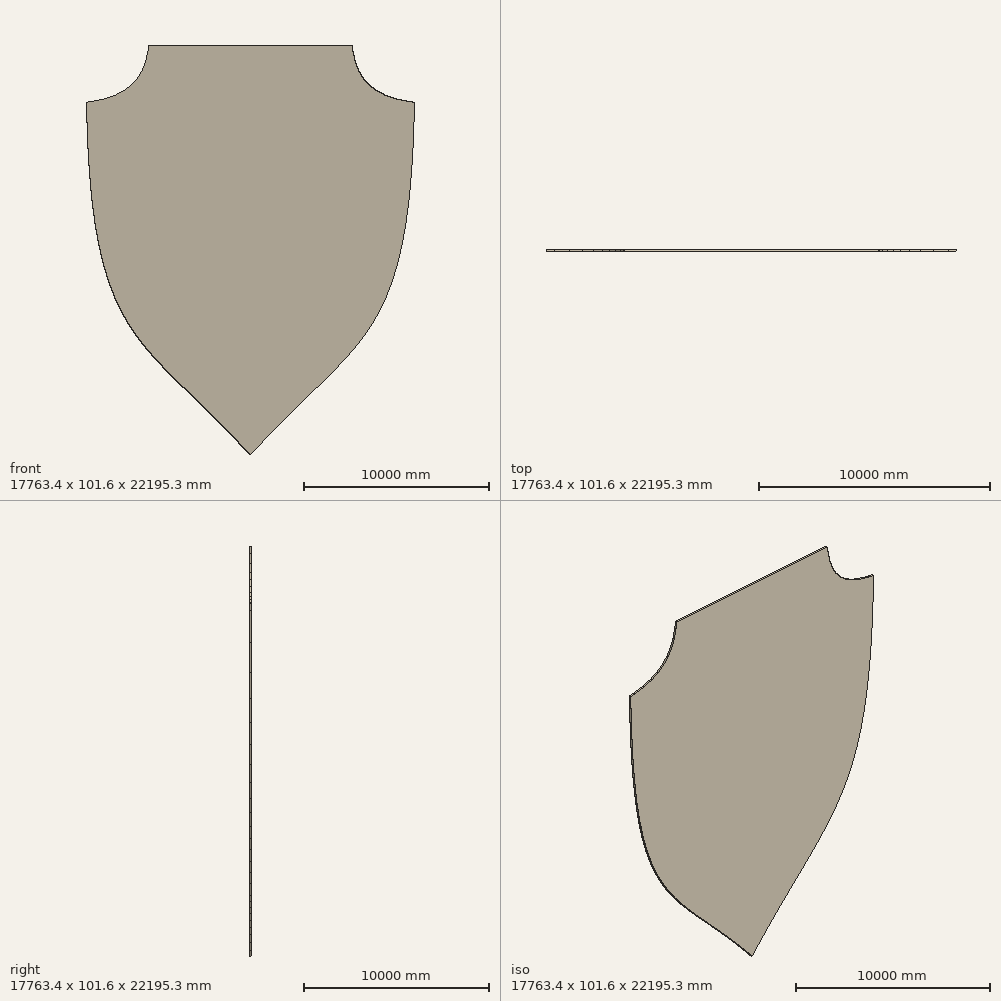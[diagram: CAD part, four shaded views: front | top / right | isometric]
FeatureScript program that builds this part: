
annotation { "Feature Type Name" : "Feature", "Feature Type Description" : "" }
export const myFeature = defineFeature(function(context is Context, id is Id, definition is map)
    precondition{}
    {
        {
            var Q0;
            Q0=qCreatedBy(makeId("Front.planeOp"),FACE);
            var sketch = newSketch(context, id + "F0", { "sketchPlane" : qUnion([Q0])});
            skLineSegment(sketch, "E0", {"start": v(3606.7, -2114.03) * mm, "end": v(3623.1, -2111.71) * mm});
            skLineSegment(sketch, "E1", {"start": v(3623.1, -2111.71) * mm, "end": v(3639.28, -2108.84) * mm});
            skLineSegment(sketch, "E2", {"start": v(3639.28, -2108.84) * mm, "end": v(3655.23, -2105.42) * mm});
            skLineSegment(sketch, "E3", {"start": v(3655.23, -2105.42) * mm, "end": v(3670.91, -2101.43) * mm});
            skLineSegment(sketch, "E4", {"start": v(3670.91, -2101.43) * mm, "end": v(3686.32, -2096.89) * mm});
            skLineSegment(sketch, "E5", {"start": v(3686.32, -2096.89) * mm, "end": v(3701.44, -2091.78) * mm});
            skLineSegment(sketch, "E6", {"start": v(3701.44, -2091.78) * mm, "end": v(3716.25, -2086.1) * mm});
            skLineSegment(sketch, "E7", {"start": v(3716.25, -2086.1) * mm, "end": v(3730.73, -2079.87) * mm});
            skLineSegment(sketch, "E8", {"start": v(3730.73, -2079.87) * mm, "end": v(3781.7, -2025.13) * mm});
            skLineSegment(sketch, "E9", {"start": v(3781.7, -2025.13) * mm, "end": v(3828.45, -1969.92) * mm});
            skLineSegment(sketch, "E10", {"start": v(3828.45, -1969.92) * mm, "end": v(3871.15, -1913.92) * mm});
            skLineSegment(sketch, "E11", {"start": v(3871.15, -1913.92) * mm, "end": v(3909.97, -1856.8) * mm});
            skLineSegment(sketch, "E12", {"start": v(3909.97, -1856.8) * mm, "end": v(3945.09, -1798.2) * mm});
            skLineSegment(sketch, "E13", {"start": v(3945.09, -1798.2) * mm, "end": v(3976.68, -1737.82) * mm});
            skLineSegment(sketch, "E14", {"start": v(3976.68, -1737.82) * mm, "end": v(4004.91, -1675.31) * mm});
            skLineSegment(sketch, "E15", {"start": v(4004.91, -1675.31) * mm, "end": v(4029.96, -1610.35) * mm});
            skLineSegment(sketch, "E16", {"start": v(4029.96, -1610.35) * mm, "end": v(4024.08, -1606.15) * mm});
            skLineSegment(sketch, "E17", {"start": v(4024.08, -1606.15) * mm, "end": v(4018.25, -1601.82) * mm});
            skLineSegment(sketch, "E18", {"start": v(4018.25, -1601.82) * mm, "end": v(4012.5, -1597.37) * mm});
            skLineSegment(sketch, "E19", {"start": v(4012.5, -1597.37) * mm, "end": v(4006.8, -1592.78) * mm});
            skLineSegment(sketch, "E20", {"start": v(4006.8, -1592.78) * mm, "end": v(4001.2, -1588.05) * mm});
            skLineSegment(sketch, "E21", {"start": v(4001.2, -1588.05) * mm, "end": v(3995.67, -1583.17) * mm});
            skLineSegment(sketch, "E22", {"start": v(3995.67, -1583.17) * mm, "end": v(3990.24, -1578.13) * mm});
            skLineSegment(sketch, "E23", {"start": v(3990.24, -1578.13) * mm, "end": v(3984.9, -1572.93) * mm});
            skLineSegment(sketch, "E24", {"start": v(3984.9, -1572.93) * mm, "end": v(3942.11, -1520.55) * mm});
            skLineSegment(sketch, "E25", {"start": v(3942.11, -1520.55) * mm, "end": v(3911.55, -1462.47) * mm});
            skLineSegment(sketch, "E26", {"start": v(3911.55, -1462.47) * mm, "end": v(3893.2, -1400.6) * mm});
            skLineSegment(sketch, "E27", {"start": v(3893.2, -1400.6) * mm, "end": v(3887.1, -1336.81) * mm});
            skLineSegment(sketch, "E28", {"start": v(3887.1, -1336.81) * mm, "end": v(3893.2, -1273.04) * mm});
            skLineSegment(sketch, "E29", {"start": v(3893.2, -1273.04) * mm, "end": v(3911.54, -1211.16) * mm});
            skLineSegment(sketch, "E30", {"start": v(3911.54, -1211.16) * mm, "end": v(3942.1, -1153.08) * mm});
            skLineSegment(sketch, "E31", {"start": v(3942.1, -1153.08) * mm, "end": v(3984.9, -1100.7) * mm});
            skLineSegment(sketch, "E32", {"start": v(3984.9, -1100.7) * mm, "end": v(4037.28, -1057.9) * mm});
            skLineSegment(sketch, "E33", {"start": v(4037.28, -1057.9) * mm, "end": v(4095.35, -1027.34) * mm});
            skLineSegment(sketch, "E34", {"start": v(4095.35, -1027.34) * mm, "end": v(4157.23, -1009) * mm});
            skLineSegment(sketch, "E35", {"start": v(4157.23, -1009) * mm, "end": v(4221, -1002.9) * mm});
            skLineSegment(sketch, "E36", {"start": v(4221, -1002.9) * mm, "end": v(4284.78, -1009) * mm});
            skLineSegment(sketch, "E37", {"start": v(4284.78, -1009) * mm, "end": v(4346.65, -1027.34) * mm});
            skLineSegment(sketch, "E38", {"start": v(4346.65, -1027.34) * mm, "end": v(4404.73, -1057.9) * mm});
            skLineSegment(sketch, "E39", {"start": v(4404.73, -1057.9) * mm, "end": v(4457.12, -1100.7) * mm});
            skLineSegment(sketch, "E40", {"start": v(4457.12, -1100.7) * mm, "end": v(4499.9, -1153.08) * mm});
            skLineSegment(sketch, "E41", {"start": v(4499.9, -1153.08) * mm, "end": v(4530.47, -1211.16) * mm});
            skLineSegment(sketch, "E42", {"start": v(4530.47, -1211.16) * mm, "end": v(4548.8, -1273.04) * mm});
            skLineSegment(sketch, "E43", {"start": v(4548.8, -1273.04) * mm, "end": v(4554.92, -1336.81) * mm});
            skLineSegment(sketch, "E44", {"start": v(4554.92, -1336.81) * mm, "end": v(4548.8, -1400.6) * mm});
            skLineSegment(sketch, "E45", {"start": v(4548.8, -1400.6) * mm, "end": v(4530.47, -1462.47) * mm});
            skLineSegment(sketch, "E46", {"start": v(4530.47, -1462.47) * mm, "end": v(4499.9, -1520.55) * mm});
            skLineSegment(sketch, "E47", {"start": v(4499.9, -1520.55) * mm, "end": v(4457.12, -1572.93) * mm});
            skLineSegment(sketch, "E48", {"start": v(4457.12, -1572.93) * mm, "end": v(4426.96, -1599.67) * mm});
            skLineSegment(sketch, "E49", {"start": v(4426.96, -1599.67) * mm, "end": v(4394.55, -1622.12) * mm});
            skLineSegment(sketch, "E50", {"start": v(4394.55, -1622.12) * mm, "end": v(4360.27, -1640.28) * mm});
            skLineSegment(sketch, "E51", {"start": v(4360.27, -1640.28) * mm, "end": v(4324.52, -1654.17) * mm});
            skLineSegment(sketch, "E52", {"start": v(4324.52, -1654.17) * mm, "end": v(4287.68, -1663.8) * mm});
            skLineSegment(sketch, "E53", {"start": v(4287.68, -1663.8) * mm, "end": v(4250.15, -1669.15) * mm});
            skLineSegment(sketch, "E54", {"start": v(4250.15, -1669.15) * mm, "end": v(4212.32, -1670.25) * mm});
            skLineSegment(sketch, "E55", {"start": v(4212.32, -1670.25) * mm, "end": v(4174.57, -1667.12) * mm});
            skLineSegment(sketch, "E56", {"start": v(4174.57, -1667.12) * mm, "end": v(4173.7, -1667.68) * mm});
            skLineSegment(sketch, "E57", {"start": v(4173.7, -1667.68) * mm, "end": v(4172.86, -1668.24) * mm});
            skLineSegment(sketch, "E58", {"start": v(4172.86, -1668.24) * mm, "end": v(4172.03, -1668.82) * mm});
            skLineSegment(sketch, "E59", {"start": v(4172.03, -1668.82) * mm, "end": v(4171.2, -1669.4) * mm});
            skLineSegment(sketch, "E60", {"start": v(4171.2, -1669.4) * mm, "end": v(4170.37, -1669.98) * mm});
            skLineSegment(sketch, "E61", {"start": v(4170.37, -1669.98) * mm, "end": v(4169.53, -1670.55) * mm});
            skLineSegment(sketch, "E62", {"start": v(4169.53, -1670.55) * mm, "end": v(4168.68, -1671.11) * mm});
            skLineSegment(sketch, "E63", {"start": v(4168.68, -1671.11) * mm, "end": v(4167.8, -1671.66) * mm});
            skLineSegment(sketch, "E64", {"start": v(4167.8, -1671.66) * mm, "end": v(4147.85, -1746.44) * mm});
            skLineSegment(sketch, "E65", {"start": v(4147.85, -1746.44) * mm, "end": v(4115.54, -1827.73) * mm});
            skLineSegment(sketch, "E66", {"start": v(4115.54, -1827.73) * mm, "end": v(4072.55, -1913.84) * mm});
            skLineSegment(sketch, "E67", {"start": v(4072.55, -1913.84) * mm, "end": v(4020.56, -2003.05) * mm});
            skLineSegment(sketch, "E68", {"start": v(4020.56, -2003.05) * mm, "end": v(3961.25, -2093.65) * mm});
            skLineSegment(sketch, "E69", {"start": v(3961.25, -2093.65) * mm, "end": v(3896.3, -2183.93) * mm});
            skLineSegment(sketch, "E70", {"start": v(3896.3, -2183.93) * mm, "end": v(3827.38, -2272.18) * mm});
            skLineSegment(sketch, "E71", {"start": v(3827.38, -2272.18) * mm, "end": v(3756.18, -2356.7) * mm});
            skLineSegment(sketch, "E72", {"start": v(3756.18, -2356.7) * mm, "end": v(4921.1, -3614.15) * mm});
            skLineSegment(sketch, "E73", {"start": v(4921.1, -3614.15) * mm, "end": v(4990.22, -3578.05) * mm});
            skLineSegment(sketch, "E74", {"start": v(4990.22, -3578.05) * mm, "end": v(5063.34, -3554.5) * mm});
            skLineSegment(sketch, "E75", {"start": v(5063.34, -3554.5) * mm, "end": v(5138.77, -3543.48) * mm});
            skLineSegment(sketch, "E76", {"start": v(5138.77, -3543.48) * mm, "end": v(5214.82, -3545.02) * mm});
            skLineSegment(sketch, "E77", {"start": v(5214.82, -3545.02) * mm, "end": v(5289.82, -3559.12) * mm});
            skLineSegment(sketch, "E78", {"start": v(5289.82, -3559.12) * mm, "end": v(5362.07, -3585.78) * mm});
            skLineSegment(sketch, "E79", {"start": v(5362.07, -3585.78) * mm, "end": v(5429.9, -3625.02) * mm});
            skLineSegment(sketch, "E80", {"start": v(5429.9, -3625.02) * mm, "end": v(5491.63, -3676.84) * mm});
            skLineSegment(sketch, "E81", {"start": v(5491.63, -3676.84) * mm, "end": v(5550.45, -3748.84) * mm});
            skLineSegment(sketch, "E82", {"start": v(5550.45, -3748.84) * mm, "end": v(5592.46, -3828.68) * mm});
            skLineSegment(sketch, "E83", {"start": v(5592.46, -3828.68) * mm, "end": v(5617.67, -3913.74) * mm});
            skLineSegment(sketch, "E84", {"start": v(5617.67, -3913.74) * mm, "end": v(5626.07, -4001.4) * mm});
            skLineSegment(sketch, "E85", {"start": v(5626.07, -4001.4) * mm, "end": v(5617.67, -4089.07) * mm});
            skLineSegment(sketch, "E86", {"start": v(5617.67, -4089.07) * mm, "end": v(5592.46, -4174.12) * mm});
            skLineSegment(sketch, "E87", {"start": v(5592.46, -4174.12) * mm, "end": v(5550.45, -4253.96) * mm});
            skLineSegment(sketch, "E88", {"start": v(5550.45, -4253.96) * mm, "end": v(5491.63, -4325.96) * mm});
            skLineSegment(sketch, "E89", {"start": v(5491.63, -4325.96) * mm, "end": v(5419.63, -4384.77) * mm});
            skLineSegment(sketch, "E90", {"start": v(5419.63, -4384.77) * mm, "end": v(5339.8, -4426.78) * mm});
            skLineSegment(sketch, "E91", {"start": v(5339.8, -4426.78) * mm, "end": v(5254.74, -4451.98) * mm});
            skLineSegment(sketch, "E92", {"start": v(5254.74, -4451.98) * mm, "end": v(5167.07, -4460.38) * mm});
            skLineSegment(sketch, "E93", {"start": v(5167.07, -4460.38) * mm, "end": v(5079.41, -4451.98) * mm});
            skLineSegment(sketch, "E94", {"start": v(5079.41, -4451.98) * mm, "end": v(4994.36, -4426.78) * mm});
            skLineSegment(sketch, "E95", {"start": v(4994.36, -4426.78) * mm, "end": v(4914.53, -4384.77) * mm});
            skLineSegment(sketch, "E96", {"start": v(4914.53, -4384.77) * mm, "end": v(4842.54, -4325.96) * mm});
            skLineSegment(sketch, "E97", {"start": v(4842.54, -4325.96) * mm, "end": v(4791.9, -4265.9) * mm});
            skLineSegment(sketch, "E98", {"start": v(4791.9, -4265.9) * mm, "end": v(4753.22, -4200.01) * mm});
            skLineSegment(sketch, "E99", {"start": v(4753.22, -4200.01) * mm, "end": v(4726.49, -4129.84) * mm});
            skLineSegment(sketch, "E100", {"start": v(4726.49, -4129.84) * mm, "end": v(4711.7, -4056.95) * mm});
            skLineSegment(sketch, "E101", {"start": v(4711.7, -4056.95) * mm, "end": v(4708.83, -3982.9) * mm});
            skLineSegment(sketch, "E102", {"start": v(4708.83, -3982.9) * mm, "end": v(4717.87, -3909.23) * mm});
            skLineSegment(sketch, "E103", {"start": v(4717.87, -3909.23) * mm, "end": v(4738.82, -3837.5) * mm});
            skLineSegment(sketch, "E104", {"start": v(4738.82, -3837.5) * mm, "end": v(4771.64, -3769.27) * mm});
            skLineSegment(sketch, "E105", {"start": v(4771.64, -3769.27) * mm, "end": v(3503.24, -2609.63) * mm});
            skLineSegment(sketch, "E106", {"start": v(3503.24, -2609.63) * mm, "end": v(3421.12, -2678.8) * mm});
            skLineSegment(sketch, "E107", {"start": v(3421.12, -2678.8) * mm, "end": v(3335.84, -2745.38) * mm});
            skLineSegment(sketch, "E108", {"start": v(3335.84, -2745.38) * mm, "end": v(3248.9, -2807.89) * mm});
            skLineSegment(sketch, "E109", {"start": v(3248.9, -2807.89) * mm, "end": v(3161.83, -2864.82) * mm});
            skLineSegment(sketch, "E110", {"start": v(3161.83, -2864.82) * mm, "end": v(3076.12, -2914.67) * mm});
            skLineSegment(sketch, "E111", {"start": v(3076.12, -2914.67) * mm, "end": v(2993.27, -2955.94) * mm});
            skLineSegment(sketch, "E112", {"start": v(2993.27, -2955.94) * mm, "end": v(2914.8, -2987.14) * mm});
            skLineSegment(sketch, "E113", {"start": v(2914.8, -2987.14) * mm, "end": v(2842.2, -3006.76) * mm});
            skLineSegment(sketch, "E114", {"start": v(2842.2, -3006.76) * mm, "end": v(2841.24, -3008.5) * mm});
            skLineSegment(sketch, "E115", {"start": v(2841.24, -3008.5) * mm, "end": v(2840.27, -3010.17) * mm});
            skLineSegment(sketch, "E116", {"start": v(2840.27, -3010.17) * mm, "end": v(2839.29, -3011.8) * mm});
            skLineSegment(sketch, "E117", {"start": v(2839.29, -3011.8) * mm, "end": v(2838.3, -3013.4) * mm});
            skLineSegment(sketch, "E118", {"start": v(2838.3, -3013.4) * mm, "end": v(2837.32, -3014.98) * mm});
            skLineSegment(sketch, "E119", {"start": v(2837.32, -3014.98) * mm, "end": v(2836.34, -3016.58) * mm});
            skLineSegment(sketch, "E120", {"start": v(2836.34, -3016.58) * mm, "end": v(2835.36, -3018.2) * mm});
            skLineSegment(sketch, "E121", {"start": v(2835.36, -3018.2) * mm, "end": v(2834.39, -3019.87) * mm});
            skLineSegment(sketch, "E122", {"start": v(2834.39, -3019.87) * mm, "end": v(2836.27, -3056.3) * mm});
            skLineSegment(sketch, "E123", {"start": v(2836.27, -3056.3) * mm, "end": v(2834.2, -3092.72) * mm});
            skLineSegment(sketch, "E124", {"start": v(2834.2, -3092.72) * mm, "end": v(2828.18, -3128.78) * mm});
            skLineSegment(sketch, "E125", {"start": v(2828.18, -3128.78) * mm, "end": v(2818.2, -3164.14) * mm});
            skLineSegment(sketch, "E126", {"start": v(2818.2, -3164.14) * mm, "end": v(2804.25, -3198.43) * mm});
            skLineSegment(sketch, "E127", {"start": v(2804.25, -3198.43) * mm, "end": v(2786.34, -3231.31) * mm});
            skLineSegment(sketch, "E128", {"start": v(2786.34, -3231.31) * mm, "end": v(2764.46, -3262.43) * mm});
            skLineSegment(sketch, "E129", {"start": v(2764.46, -3262.43) * mm, "end": v(2738.6, -3291.45) * mm});
            skLineSegment(sketch, "E130", {"start": v(2738.6, -3291.45) * mm, "end": v(2686.22, -3334.23) * mm});
            skLineSegment(sketch, "E131", {"start": v(2686.22, -3334.23) * mm, "end": v(2628.14, -3364.8) * mm});
            skLineSegment(sketch, "E132", {"start": v(2628.14, -3364.8) * mm, "end": v(2566.26, -3383.13) * mm});
            skLineSegment(sketch, "E133", {"start": v(2566.26, -3383.13) * mm, "end": v(2502.49, -3389.24) * mm});
            skLineSegment(sketch, "E134", {"start": v(2502.49, -3389.24) * mm, "end": v(2438.71, -3383.13) * mm});
            skLineSegment(sketch, "E135", {"start": v(2438.71, -3383.13) * mm, "end": v(2376.84, -3364.79) * mm});
            skLineSegment(sketch, "E136", {"start": v(2376.84, -3364.79) * mm, "end": v(2318.77, -3334.23) * mm});
            skLineSegment(sketch, "E137", {"start": v(2318.77, -3334.23) * mm, "end": v(2266.4, -3291.45) * mm});
            skLineSegment(sketch, "E138", {"start": v(2266.4, -3291.45) * mm, "end": v(2223.6, -3239.06) * mm});
            skLineSegment(sketch, "E139", {"start": v(2223.6, -3239.06) * mm, "end": v(2193.04, -3180.98) * mm});
            skLineSegment(sketch, "E140", {"start": v(2193.04, -3180.98) * mm, "end": v(2174.7, -3119.1) * mm});
            skLineSegment(sketch, "E141", {"start": v(2174.7, -3119.1) * mm, "end": v(2168.59, -3055.33) * mm});
            skLineSegment(sketch, "E142", {"start": v(2168.59, -3055.33) * mm, "end": v(2174.7, -2991.55) * mm});
            skLineSegment(sketch, "E143", {"start": v(2174.7, -2991.55) * mm, "end": v(2193.04, -2929.67) * mm});
            skLineSegment(sketch, "E144", {"start": v(2193.04, -2929.67) * mm, "end": v(2223.6, -2871.6) * mm});
            skLineSegment(sketch, "E145", {"start": v(2223.6, -2871.6) * mm, "end": v(2266.4, -2819.2) * mm});
            skLineSegment(sketch, "E146", {"start": v(2266.4, -2819.2) * mm, "end": v(2318.77, -2776.42) * mm});
            skLineSegment(sketch, "E147", {"start": v(2318.77, -2776.42) * mm, "end": v(2376.84, -2745.86) * mm});
            skLineSegment(sketch, "E148", {"start": v(2376.84, -2745.86) * mm, "end": v(2438.71, -2727.52) * mm});
            skLineSegment(sketch, "E149", {"start": v(2438.71, -2727.52) * mm, "end": v(2502.49, -2721.4) * mm});
            skLineSegment(sketch, "E150", {"start": v(2502.49, -2721.4) * mm, "end": v(2566.26, -2727.52) * mm});
            skLineSegment(sketch, "E151", {"start": v(2566.26, -2727.52) * mm, "end": v(2628.14, -2745.86) * mm});
            skLineSegment(sketch, "E152", {"start": v(2628.14, -2745.86) * mm, "end": v(2686.22, -2776.42) * mm});
            skLineSegment(sketch, "E153", {"start": v(2686.22, -2776.42) * mm, "end": v(2738.6, -2819.2) * mm});
            skLineSegment(sketch, "E154", {"start": v(2738.6, -2819.2) * mm, "end": v(2741.5, -2822.14) * mm});
            skLineSegment(sketch, "E155", {"start": v(2741.5, -2822.14) * mm, "end": v(2744.33, -2825.1) * mm});
            skLineSegment(sketch, "E156", {"start": v(2744.33, -2825.1) * mm, "end": v(2747.12, -2828.08) * mm});
            skLineSegment(sketch, "E157", {"start": v(2747.12, -2828.08) * mm, "end": v(2749.86, -2831.09) * mm});
            skLineSegment(sketch, "E158", {"start": v(2749.86, -2831.09) * mm, "end": v(2752.56, -2834.12) * mm});
            skLineSegment(sketch, "E159", {"start": v(2752.56, -2834.12) * mm, "end": v(2755.22, -2837.18) * mm});
            skLineSegment(sketch, "E160", {"start": v(2755.22, -2837.18) * mm, "end": v(2757.84, -2840.26) * mm});
            skLineSegment(sketch, "E161", {"start": v(2757.84, -2840.26) * mm, "end": v(2760.42, -2843.36) * mm});
            skLineSegment(sketch, "E162", {"start": v(2760.42, -2843.36) * mm, "end": v(2762.04, -2844.08) * mm});
            skLineSegment(sketch, "E163", {"start": v(2762.04, -2844.08) * mm, "end": v(2763.64, -2844.76) * mm});
            skLineSegment(sketch, "E164", {"start": v(2763.64, -2844.76) * mm, "end": v(2765.24, -2845.41) * mm});
            skLineSegment(sketch, "E165", {"start": v(2765.24, -2845.41) * mm, "end": v(2766.84, -2846.06) * mm});
            skLineSegment(sketch, "E166", {"start": v(2766.84, -2846.06) * mm, "end": v(2768.44, -2846.71) * mm});
            skLineSegment(sketch, "E167", {"start": v(2768.44, -2846.71) * mm, "end": v(2770.04, -2847.4) * mm});
            skLineSegment(sketch, "E168", {"start": v(2770.04, -2847.4) * mm, "end": v(2771.65, -2848.12) * mm});
            skLineSegment(sketch, "E169", {"start": v(2771.65, -2848.12) * mm, "end": v(2773.27, -2848.9) * mm});
            skLineSegment(sketch, "E170", {"start": v(2773.27, -2848.9) * mm, "end": v(2844.85, -2823.3) * mm});
            skLineSegment(sketch, "E171", {"start": v(2844.85, -2823.3) * mm, "end": v(2913.29, -2794.08) * mm});
            skLineSegment(sketch, "E172", {"start": v(2913.29, -2794.08) * mm, "end": v(2979.01, -2761.05) * mm});
            skLineSegment(sketch, "E173", {"start": v(2979.01, -2761.05) * mm, "end": v(3042.46, -2723.98) * mm});
            skLineSegment(sketch, "E174", {"start": v(3042.46, -2723.98) * mm, "end": v(3104.07, -2682.7) * mm});
            skLineSegment(sketch, "E175", {"start": v(3104.07, -2682.7) * mm, "end": v(3164.27, -2636.97) * mm});
            skLineSegment(sketch, "E176", {"start": v(3164.27, -2636.97) * mm, "end": v(3223.49, -2586.6) * mm});
            skLineSegment(sketch, "E177", {"start": v(3223.49, -2586.6) * mm, "end": v(3282.16, -2531.4) * mm});
            skLineSegment(sketch, "E178", {"start": v(3282.16, -2531.4) * mm, "end": v(3285.99, -2522.54) * mm});
            skLineSegment(sketch, "E179", {"start": v(3285.99, -2522.54) * mm, "end": v(3289.6, -2513.54) * mm});
            skLineSegment(sketch, "E180", {"start": v(3289.6, -2513.54) * mm, "end": v(3292.98, -2504.42) * mm});
            skLineSegment(sketch, "E181", {"start": v(3292.98, -2504.42) * mm, "end": v(3296.16, -2495.2) * mm});
            skLineSegment(sketch, "E182", {"start": v(3296.16, -2495.2) * mm, "end": v(3299.14, -2485.85) * mm});
            skLineSegment(sketch, "E183", {"start": v(3299.14, -2485.85) * mm, "end": v(3301.9, -2476.4) * mm});
            skLineSegment(sketch, "E184", {"start": v(3301.9, -2476.4) * mm, "end": v(3304.48, -2466.85) * mm});
            skLineSegment(sketch, "E185", {"start": v(3304.48, -2466.85) * mm, "end": v(3306.85, -2457.2) * mm});
            skLineSegment(sketch, "E186", {"start": v(3306.85, -2457.2) * mm, "end": v(3195.62, -2346.67) * mm});
            skLineSegment(sketch, "E187", {"start": v(3195.62, -2346.67) * mm, "end": v(3195.63, -2346.65) * mm});
            skLineSegment(sketch, "E188", {"start": v(3195.63, -2346.65) * mm, "end": v(3195.64, -2346.59) * mm});
            skLineSegment(sketch, "E189", {"start": v(3195.64, -2346.59) * mm, "end": v(3195.66, -2346.5) * mm});
            skLineSegment(sketch, "E190", {"start": v(3195.66, -2346.5) * mm, "end": v(3195.69, -2346.41) * mm});
            skLineSegment(sketch, "E191", {"start": v(3195.69, -2346.41) * mm, "end": v(3195.71, -2346.32) * mm});
            skLineSegment(sketch, "E192", {"start": v(3195.71, -2346.32) * mm, "end": v(3195.73, -2346.24) * mm});
            skLineSegment(sketch, "E193", {"start": v(3195.73, -2346.24) * mm, "end": v(3195.75, -2346.18) * mm});
            skLineSegment(sketch, "E194", {"start": v(3195.75, -2346.18) * mm, "end": v(3195.75, -2346.16) * mm});
            skLineSegment(sketch, "E195", {"start": v(3195.75, -2346.16) * mm, "end": v(0, 830.72) * mm});
            skLineSegment(sketch, "E196", {"start": v(0, 830.72) * mm, "end": v(-3195.75, -2346.16) * mm});
            skLineSegment(sketch, "E197", {"start": v(-3195.75, -2346.16) * mm, "end": v(-3195.75, -2346.18) * mm});
            skLineSegment(sketch, "E198", {"start": v(-3195.75, -2346.18) * mm, "end": v(-3195.73, -2346.24) * mm});
            skLineSegment(sketch, "E199", {"start": v(-3195.73, -2346.24) * mm, "end": v(-3195.71, -2346.32) * mm});
            skLineSegment(sketch, "E200", {"start": v(-3195.71, -2346.32) * mm, "end": v(-3195.69, -2346.41) * mm});
            skLineSegment(sketch, "E201", {"start": v(-3195.69, -2346.41) * mm, "end": v(-3195.66, -2346.5) * mm});
            skLineSegment(sketch, "E202", {"start": v(-3195.66, -2346.5) * mm, "end": v(-3195.64, -2346.59) * mm});
            skLineSegment(sketch, "E203", {"start": v(-3195.64, -2346.59) * mm, "end": v(-3195.63, -2346.65) * mm});
            skLineSegment(sketch, "E204", {"start": v(-3195.63, -2346.65) * mm, "end": v(-3195.62, -2346.67) * mm});
            skLineSegment(sketch, "E205", {"start": v(-3195.62, -2346.67) * mm, "end": v(-3306.85, -2457.2) * mm});
            skLineSegment(sketch, "E206", {"start": v(-3306.85, -2457.2) * mm, "end": v(-3304.48, -2466.85) * mm});
            skLineSegment(sketch, "E207", {"start": v(-3304.48, -2466.85) * mm, "end": v(-3301.9, -2476.4) * mm});
            skLineSegment(sketch, "E208", {"start": v(-3301.9, -2476.4) * mm, "end": v(-3299.14, -2485.85) * mm});
            skLineSegment(sketch, "E209", {"start": v(-3299.14, -2485.85) * mm, "end": v(-3296.16, -2495.2) * mm});
            skLineSegment(sketch, "E210", {"start": v(-3296.16, -2495.2) * mm, "end": v(-3292.98, -2504.42) * mm});
            skLineSegment(sketch, "E211", {"start": v(-3292.98, -2504.42) * mm, "end": v(-3289.6, -2513.54) * mm});
            skLineSegment(sketch, "E212", {"start": v(-3289.6, -2513.54) * mm, "end": v(-3285.99, -2522.54) * mm});
            skLineSegment(sketch, "E213", {"start": v(-3285.99, -2522.54) * mm, "end": v(-3282.16, -2531.4) * mm});
            skLineSegment(sketch, "E214", {"start": v(-3282.16, -2531.4) * mm, "end": v(-3223.49, -2586.6) * mm});
            skLineSegment(sketch, "E215", {"start": v(-3223.49, -2586.6) * mm, "end": v(-3164.27, -2636.97) * mm});
            skLineSegment(sketch, "E216", {"start": v(-3164.27, -2636.97) * mm, "end": v(-3104.07, -2682.7) * mm});
            skLineSegment(sketch, "E217", {"start": v(-3104.07, -2682.7) * mm, "end": v(-3042.46, -2723.98) * mm});
            skLineSegment(sketch, "E218", {"start": v(-3042.46, -2723.98) * mm, "end": v(-2979.01, -2761.05) * mm});
            skLineSegment(sketch, "E219", {"start": v(-2979.01, -2761.05) * mm, "end": v(-2913.29, -2794.08) * mm});
            skLineSegment(sketch, "E220", {"start": v(-2913.29, -2794.08) * mm, "end": v(-2844.85, -2823.3) * mm});
            skLineSegment(sketch, "E221", {"start": v(-2844.85, -2823.3) * mm, "end": v(-2773.27, -2848.9) * mm});
            skLineSegment(sketch, "E222", {"start": v(-2773.27, -2848.9) * mm, "end": v(-2771.65, -2848.12) * mm});
            skLineSegment(sketch, "E223", {"start": v(-2771.65, -2848.12) * mm, "end": v(-2770.04, -2847.4) * mm});
            skLineSegment(sketch, "E224", {"start": v(-2770.04, -2847.4) * mm, "end": v(-2768.44, -2846.71) * mm});
            skLineSegment(sketch, "E225", {"start": v(-2768.44, -2846.71) * mm, "end": v(-2766.84, -2846.06) * mm});
            skLineSegment(sketch, "E226", {"start": v(-2766.84, -2846.06) * mm, "end": v(-2765.24, -2845.41) * mm});
            skLineSegment(sketch, "E227", {"start": v(-2765.24, -2845.41) * mm, "end": v(-2763.64, -2844.76) * mm});
            skLineSegment(sketch, "E228", {"start": v(-2763.64, -2844.76) * mm, "end": v(-2762.04, -2844.08) * mm});
            skLineSegment(sketch, "E229", {"start": v(-2762.04, -2844.08) * mm, "end": v(-2760.42, -2843.36) * mm});
            skLineSegment(sketch, "E230", {"start": v(-2760.42, -2843.36) * mm, "end": v(-2757.84, -2840.26) * mm});
            skLineSegment(sketch, "E231", {"start": v(-2757.84, -2840.26) * mm, "end": v(-2755.22, -2837.18) * mm});
            skLineSegment(sketch, "E232", {"start": v(-2755.22, -2837.18) * mm, "end": v(-2752.56, -2834.12) * mm});
            skLineSegment(sketch, "E233", {"start": v(-2752.56, -2834.12) * mm, "end": v(-2749.85, -2831.09) * mm});
            skLineSegment(sketch, "E234", {"start": v(-2749.85, -2831.09) * mm, "end": v(-2747.1, -2828.08) * mm});
            skLineSegment(sketch, "E235", {"start": v(-2747.1, -2828.08) * mm, "end": v(-2744.32, -2825.1) * mm});
            skLineSegment(sketch, "E236", {"start": v(-2744.32, -2825.1) * mm, "end": v(-2741.48, -2822.14) * mm});
            skLineSegment(sketch, "E237", {"start": v(-2741.48, -2822.14) * mm, "end": v(-2738.6, -2819.2) * mm});
            skLineSegment(sketch, "E238", {"start": v(-2738.6, -2819.2) * mm, "end": v(-2686.22, -2776.42) * mm});
            skLineSegment(sketch, "E239", {"start": v(-2686.22, -2776.42) * mm, "end": v(-2628.14, -2745.86) * mm});
            skLineSegment(sketch, "E240", {"start": v(-2628.14, -2745.86) * mm, "end": v(-2566.26, -2727.52) * mm});
            skLineSegment(sketch, "E241", {"start": v(-2566.26, -2727.52) * mm, "end": v(-2502.48, -2721.4) * mm});
            skLineSegment(sketch, "E242", {"start": v(-2502.48, -2721.4) * mm, "end": v(-2438.7, -2727.52) * mm});
            skLineSegment(sketch, "E243", {"start": v(-2438.7, -2727.52) * mm, "end": v(-2376.83, -2745.86) * mm});
            skLineSegment(sketch, "E244", {"start": v(-2376.83, -2745.86) * mm, "end": v(-2318.75, -2776.42) * mm});
            skLineSegment(sketch, "E245", {"start": v(-2318.75, -2776.42) * mm, "end": v(-2266.37, -2819.2) * mm});
            skLineSegment(sketch, "E246", {"start": v(-2266.37, -2819.2) * mm, "end": v(-2223.59, -2871.6) * mm});
            skLineSegment(sketch, "E247", {"start": v(-2223.59, -2871.6) * mm, "end": v(-2193.03, -2929.67) * mm});
            skLineSegment(sketch, "E248", {"start": v(-2193.03, -2929.67) * mm, "end": v(-2174.7, -2991.55) * mm});
            skLineSegment(sketch, "E249", {"start": v(-2174.7, -2991.55) * mm, "end": v(-2168.58, -3055.33) * mm});
            skLineSegment(sketch, "E250", {"start": v(-2168.58, -3055.33) * mm, "end": v(-2174.7, -3119.1) * mm});
            skLineSegment(sketch, "E251", {"start": v(-2174.7, -3119.1) * mm, "end": v(-2193.03, -3180.98) * mm});
            skLineSegment(sketch, "E252", {"start": v(-2193.03, -3180.98) * mm, "end": v(-2223.59, -3239.06) * mm});
            skLineSegment(sketch, "E253", {"start": v(-2223.59, -3239.06) * mm, "end": v(-2266.37, -3291.45) * mm});
            skLineSegment(sketch, "E254", {"start": v(-2266.37, -3291.45) * mm, "end": v(-2318.75, -3334.23) * mm});
            skLineSegment(sketch, "E255", {"start": v(-2318.75, -3334.23) * mm, "end": v(-2376.83, -3364.79) * mm});
            skLineSegment(sketch, "E256", {"start": v(-2376.83, -3364.79) * mm, "end": v(-2438.7, -3383.13) * mm});
            skLineSegment(sketch, "E257", {"start": v(-2438.7, -3383.13) * mm, "end": v(-2502.48, -3389.24) * mm});
            skLineSegment(sketch, "E258", {"start": v(-2502.48, -3389.24) * mm, "end": v(-2566.26, -3383.13) * mm});
            skLineSegment(sketch, "E259", {"start": v(-2566.26, -3383.13) * mm, "end": v(-2628.14, -3364.8) * mm});
            skLineSegment(sketch, "E260", {"start": v(-2628.14, -3364.8) * mm, "end": v(-2686.22, -3334.23) * mm});
            skLineSegment(sketch, "E261", {"start": v(-2686.22, -3334.23) * mm, "end": v(-2738.6, -3291.45) * mm});
            skLineSegment(sketch, "E262", {"start": v(-2738.6, -3291.45) * mm, "end": v(-2764.46, -3262.43) * mm});
            skLineSegment(sketch, "E263", {"start": v(-2764.46, -3262.43) * mm, "end": v(-2786.34, -3231.31) * mm});
            skLineSegment(sketch, "E264", {"start": v(-2786.34, -3231.31) * mm, "end": v(-2804.25, -3198.43) * mm});
            skLineSegment(sketch, "E265", {"start": v(-2804.25, -3198.43) * mm, "end": v(-2818.2, -3164.14) * mm});
            skLineSegment(sketch, "E266", {"start": v(-2818.2, -3164.14) * mm, "end": v(-2828.18, -3128.78) * mm});
            skLineSegment(sketch, "E267", {"start": v(-2828.18, -3128.78) * mm, "end": v(-2834.2, -3092.72) * mm});
            skLineSegment(sketch, "E268", {"start": v(-2834.2, -3092.72) * mm, "end": v(-2836.27, -3056.3) * mm});
            skLineSegment(sketch, "E269", {"start": v(-2836.27, -3056.3) * mm, "end": v(-2834.39, -3019.87) * mm});
            skLineSegment(sketch, "E270", {"start": v(-2834.39, -3019.87) * mm, "end": v(-2835.36, -3018.2) * mm});
            skLineSegment(sketch, "E271", {"start": v(-2835.36, -3018.2) * mm, "end": v(-2836.34, -3016.58) * mm});
            skLineSegment(sketch, "E272", {"start": v(-2836.34, -3016.58) * mm, "end": v(-2837.32, -3014.98) * mm});
            skLineSegment(sketch, "E273", {"start": v(-2837.32, -3014.98) * mm, "end": v(-2838.3, -3013.4) * mm});
            skLineSegment(sketch, "E274", {"start": v(-2838.3, -3013.4) * mm, "end": v(-2839.29, -3011.8) * mm});
            skLineSegment(sketch, "E275", {"start": v(-2839.29, -3011.8) * mm, "end": v(-2840.27, -3010.17) * mm});
            skLineSegment(sketch, "E276", {"start": v(-2840.27, -3010.17) * mm, "end": v(-2841.24, -3008.5) * mm});
            skLineSegment(sketch, "E277", {"start": v(-2841.24, -3008.5) * mm, "end": v(-2842.2, -3006.76) * mm});
            skLineSegment(sketch, "E278", {"start": v(-2842.2, -3006.76) * mm, "end": v(-2914.8, -2987.14) * mm});
            skLineSegment(sketch, "E279", {"start": v(-2914.8, -2987.14) * mm, "end": v(-2993.27, -2955.94) * mm});
            skLineSegment(sketch, "E280", {"start": v(-2993.27, -2955.94) * mm, "end": v(-3076.12, -2914.67) * mm});
            skLineSegment(sketch, "E281", {"start": v(-3076.12, -2914.67) * mm, "end": v(-3161.83, -2864.82) * mm});
            skLineSegment(sketch, "E282", {"start": v(-3161.83, -2864.82) * mm, "end": v(-3248.9, -2807.89) * mm});
            skLineSegment(sketch, "E283", {"start": v(-3248.9, -2807.89) * mm, "end": v(-3335.84, -2745.38) * mm});
            skLineSegment(sketch, "E284", {"start": v(-3335.84, -2745.38) * mm, "end": v(-3421.12, -2678.8) * mm});
            skLineSegment(sketch, "E285", {"start": v(-3421.12, -2678.8) * mm, "end": v(-3503.24, -2609.63) * mm});
            skLineSegment(sketch, "E286", {"start": v(-3503.24, -2609.63) * mm, "end": v(-4771.62, -3769.27) * mm});
            skLineSegment(sketch, "E287", {"start": v(-4771.62, -3769.27) * mm, "end": v(-4738.8, -3837.5) * mm});
            skLineSegment(sketch, "E288", {"start": v(-4738.8, -3837.5) * mm, "end": v(-4717.86, -3909.23) * mm});
            skLineSegment(sketch, "E289", {"start": v(-4717.86, -3909.23) * mm, "end": v(-4708.82, -3982.9) * mm});
            skLineSegment(sketch, "E290", {"start": v(-4708.82, -3982.9) * mm, "end": v(-4711.7, -4056.95) * mm});
            skLineSegment(sketch, "E291", {"start": v(-4711.7, -4056.95) * mm, "end": v(-4726.48, -4129.84) * mm});
            skLineSegment(sketch, "E292", {"start": v(-4726.48, -4129.84) * mm, "end": v(-4753.2, -4200.01) * mm});
            skLineSegment(sketch, "E293", {"start": v(-4753.2, -4200.01) * mm, "end": v(-4791.88, -4265.9) * mm});
            skLineSegment(sketch, "E294", {"start": v(-4791.88, -4265.9) * mm, "end": v(-4842.51, -4325.96) * mm});
            skLineSegment(sketch, "E295", {"start": v(-4842.51, -4325.96) * mm, "end": v(-4914.51, -4384.77) * mm});
            skLineSegment(sketch, "E296", {"start": v(-4914.51, -4384.77) * mm, "end": v(-4994.35, -4426.78) * mm});
            skLineSegment(sketch, "E297", {"start": v(-4994.35, -4426.78) * mm, "end": v(-5079.4, -4451.98) * mm});
            skLineSegment(sketch, "E298", {"start": v(-5079.4, -4451.98) * mm, "end": v(-5167.07, -4460.38) * mm});
            skLineSegment(sketch, "E299", {"start": v(-5167.07, -4460.38) * mm, "end": v(-5254.74, -4451.98) * mm});
            skLineSegment(sketch, "E300", {"start": v(-5254.74, -4451.98) * mm, "end": v(-5339.8, -4426.78) * mm});
            skLineSegment(sketch, "E301", {"start": v(-5339.8, -4426.78) * mm, "end": v(-5419.63, -4384.77) * mm});
            skLineSegment(sketch, "E302", {"start": v(-5419.63, -4384.77) * mm, "end": v(-5491.63, -4325.96) * mm});
            skLineSegment(sketch, "E303", {"start": v(-5491.63, -4325.96) * mm, "end": v(-5550.45, -4253.96) * mm});
            skLineSegment(sketch, "E304", {"start": v(-5550.45, -4253.96) * mm, "end": v(-5592.46, -4174.12) * mm});
            skLineSegment(sketch, "E305", {"start": v(-5592.46, -4174.12) * mm, "end": v(-5617.67, -4089.07) * mm});
            skLineSegment(sketch, "E306", {"start": v(-5617.67, -4089.07) * mm, "end": v(-5626.07, -4001.4) * mm});
            skLineSegment(sketch, "E307", {"start": v(-5626.07, -4001.4) * mm, "end": v(-5617.67, -3913.74) * mm});
            skLineSegment(sketch, "E308", {"start": v(-5617.67, -3913.74) * mm, "end": v(-5592.46, -3828.68) * mm});
            skLineSegment(sketch, "E309", {"start": v(-5592.46, -3828.68) * mm, "end": v(-5550.45, -3748.84) * mm});
            skLineSegment(sketch, "E310", {"start": v(-5550.45, -3748.84) * mm, "end": v(-5491.63, -3676.84) * mm});
            skLineSegment(sketch, "E311", {"start": v(-5491.63, -3676.84) * mm, "end": v(-5429.9, -3625.02) * mm});
            skLineSegment(sketch, "E312", {"start": v(-5429.9, -3625.02) * mm, "end": v(-5362.07, -3585.78) * mm});
            skLineSegment(sketch, "E313", {"start": v(-5362.07, -3585.78) * mm, "end": v(-5289.81, -3559.12) * mm});
            skLineSegment(sketch, "E314", {"start": v(-5289.81, -3559.12) * mm, "end": v(-5214.81, -3545.02) * mm});
            skLineSegment(sketch, "E315", {"start": v(-5214.81, -3545.02) * mm, "end": v(-5138.76, -3543.48) * mm});
            skLineSegment(sketch, "E316", {"start": v(-5138.76, -3543.48) * mm, "end": v(-5063.33, -3554.5) * mm});
            skLineSegment(sketch, "E317", {"start": v(-5063.33, -3554.5) * mm, "end": v(-4990.22, -3578.05) * mm});
            skLineSegment(sketch, "E318", {"start": v(-4990.22, -3578.05) * mm, "end": v(-4921.1, -3614.15) * mm});
            skLineSegment(sketch, "E319", {"start": v(-4921.1, -3614.15) * mm, "end": v(-3756.18, -2356.7) * mm});
            skLineSegment(sketch, "E320", {"start": v(-3756.18, -2356.7) * mm, "end": v(-3827.38, -2272.18) * mm});
            skLineSegment(sketch, "E321", {"start": v(-3827.38, -2272.18) * mm, "end": v(-3896.3, -2183.93) * mm});
            skLineSegment(sketch, "E322", {"start": v(-3896.3, -2183.93) * mm, "end": v(-3961.25, -2093.65) * mm});
            skLineSegment(sketch, "E323", {"start": v(-3961.25, -2093.65) * mm, "end": v(-4020.55, -2003.05) * mm});
            skLineSegment(sketch, "E324", {"start": v(-4020.55, -2003.05) * mm, "end": v(-4072.53, -1913.84) * mm});
            skLineSegment(sketch, "E325", {"start": v(-4072.53, -1913.84) * mm, "end": v(-4115.52, -1827.73) * mm});
            skLineSegment(sketch, "E326", {"start": v(-4115.52, -1827.73) * mm, "end": v(-4147.83, -1746.44) * mm});
            skLineSegment(sketch, "E327", {"start": v(-4147.83, -1746.44) * mm, "end": v(-4167.78, -1671.66) * mm});
            skLineSegment(sketch, "E328", {"start": v(-4167.78, -1671.66) * mm, "end": v(-4168.66, -1671.11) * mm});
            skLineSegment(sketch, "E329", {"start": v(-4168.66, -1671.11) * mm, "end": v(-4169.52, -1670.55) * mm});
            skLineSegment(sketch, "E330", {"start": v(-4169.52, -1670.55) * mm, "end": v(-4170.36, -1669.98) * mm});
            skLineSegment(sketch, "E331", {"start": v(-4170.36, -1669.98) * mm, "end": v(-4171.2, -1669.4) * mm});
            skLineSegment(sketch, "E332", {"start": v(-4171.2, -1669.4) * mm, "end": v(-4172.03, -1668.82) * mm});
            skLineSegment(sketch, "E333", {"start": v(-4172.03, -1668.82) * mm, "end": v(-4172.86, -1668.24) * mm});
            skLineSegment(sketch, "E334", {"start": v(-4172.86, -1668.24) * mm, "end": v(-4173.7, -1667.68) * mm});
            skLineSegment(sketch, "E335", {"start": v(-4173.7, -1667.68) * mm, "end": v(-4174.57, -1667.12) * mm});
            skLineSegment(sketch, "E336", {"start": v(-4174.57, -1667.12) * mm, "end": v(-4212.32, -1670.25) * mm});
            skLineSegment(sketch, "E337", {"start": v(-4212.32, -1670.25) * mm, "end": v(-4250.15, -1669.15) * mm});
            skLineSegment(sketch, "E338", {"start": v(-4250.15, -1669.15) * mm, "end": v(-4287.68, -1663.8) * mm});
            skLineSegment(sketch, "E339", {"start": v(-4287.68, -1663.8) * mm, "end": v(-4324.52, -1654.17) * mm});
            skLineSegment(sketch, "E340", {"start": v(-4324.52, -1654.17) * mm, "end": v(-4360.27, -1640.28) * mm});
            skLineSegment(sketch, "E341", {"start": v(-4360.27, -1640.28) * mm, "end": v(-4394.55, -1622.12) * mm});
            skLineSegment(sketch, "E342", {"start": v(-4394.55, -1622.12) * mm, "end": v(-4426.96, -1599.67) * mm});
            skLineSegment(sketch, "E343", {"start": v(-4426.96, -1599.67) * mm, "end": v(-4457.12, -1572.93) * mm});
            skLineSegment(sketch, "E344", {"start": v(-4457.12, -1572.93) * mm, "end": v(-4499.9, -1520.55) * mm});
            skLineSegment(sketch, "E345", {"start": v(-4499.9, -1520.55) * mm, "end": v(-4530.47, -1462.47) * mm});
            skLineSegment(sketch, "E346", {"start": v(-4530.47, -1462.47) * mm, "end": v(-4548.8, -1400.6) * mm});
            skLineSegment(sketch, "E347", {"start": v(-4548.8, -1400.6) * mm, "end": v(-4554.92, -1336.81) * mm});
            skLineSegment(sketch, "E348", {"start": v(-4554.92, -1336.81) * mm, "end": v(-4548.8, -1273.04) * mm});
            skLineSegment(sketch, "E349", {"start": v(-4548.8, -1273.04) * mm, "end": v(-4530.47, -1211.16) * mm});
            skLineSegment(sketch, "E350", {"start": v(-4530.47, -1211.16) * mm, "end": v(-4499.9, -1153.08) * mm});
            skLineSegment(sketch, "E351", {"start": v(-4499.9, -1153.08) * mm, "end": v(-4457.12, -1100.7) * mm});
            skLineSegment(sketch, "E352", {"start": v(-4457.12, -1100.7) * mm, "end": v(-4404.73, -1057.9) * mm});
            skLineSegment(sketch, "E353", {"start": v(-4404.73, -1057.9) * mm, "end": v(-4346.65, -1027.34) * mm});
            skLineSegment(sketch, "E354", {"start": v(-4346.65, -1027.34) * mm, "end": v(-4284.77, -1009) * mm});
            skLineSegment(sketch, "E355", {"start": v(-4284.77, -1009) * mm, "end": v(-4221, -1002.9) * mm});
            skLineSegment(sketch, "E356", {"start": v(-4221, -1002.9) * mm, "end": v(-4157.22, -1009) * mm});
            skLineSegment(sketch, "E357", {"start": v(-4157.22, -1009) * mm, "end": v(-4095.34, -1027.34) * mm});
            skLineSegment(sketch, "E358", {"start": v(-4095.34, -1027.34) * mm, "end": v(-4037.26, -1057.9) * mm});
            skLineSegment(sketch, "E359", {"start": v(-4037.26, -1057.9) * mm, "end": v(-3984.88, -1100.7) * mm});
            skLineSegment(sketch, "E360", {"start": v(-3984.88, -1100.7) * mm, "end": v(-3942.1, -1153.08) * mm});
            skLineSegment(sketch, "E361", {"start": v(-3942.1, -1153.08) * mm, "end": v(-3911.53, -1211.16) * mm});
            skLineSegment(sketch, "E362", {"start": v(-3911.53, -1211.16) * mm, "end": v(-3893.19, -1273.04) * mm});
            skLineSegment(sketch, "E363", {"start": v(-3893.19, -1273.04) * mm, "end": v(-3887.08, -1336.81) * mm});
            skLineSegment(sketch, "E364", {"start": v(-3887.08, -1336.81) * mm, "end": v(-3893.19, -1400.6) * mm});
            skLineSegment(sketch, "E365", {"start": v(-3893.19, -1400.6) * mm, "end": v(-3911.53, -1462.47) * mm});
            skLineSegment(sketch, "E366", {"start": v(-3911.53, -1462.47) * mm, "end": v(-3942.1, -1520.55) * mm});
            skLineSegment(sketch, "E367", {"start": v(-3942.1, -1520.55) * mm, "end": v(-3984.88, -1572.93) * mm});
            skLineSegment(sketch, "E368", {"start": v(-3984.88, -1572.93) * mm, "end": v(-3990.22, -1578.13) * mm});
            skLineSegment(sketch, "E369", {"start": v(-3990.22, -1578.13) * mm, "end": v(-3995.65, -1583.17) * mm});
            skLineSegment(sketch, "E370", {"start": v(-3995.65, -1583.17) * mm, "end": v(-4001.18, -1588.05) * mm});
            skLineSegment(sketch, "E371", {"start": v(-4001.18, -1588.05) * mm, "end": v(-4006.8, -1592.78) * mm});
            skLineSegment(sketch, "E372", {"start": v(-4006.8, -1592.78) * mm, "end": v(-4012.48, -1597.37) * mm});
            skLineSegment(sketch, "E373", {"start": v(-4012.48, -1597.37) * mm, "end": v(-4018.25, -1601.82) * mm});
            skLineSegment(sketch, "E374", {"start": v(-4018.25, -1601.82) * mm, "end": v(-4024.08, -1606.15) * mm});
            skLineSegment(sketch, "E375", {"start": v(-4024.08, -1606.15) * mm, "end": v(-4029.96, -1610.35) * mm});
            skLineSegment(sketch, "E376", {"start": v(-4029.96, -1610.35) * mm, "end": v(-4004.91, -1675.31) * mm});
            skLineSegment(sketch, "E377", {"start": v(-4004.91, -1675.31) * mm, "end": v(-3976.68, -1737.82) * mm});
            skLineSegment(sketch, "E378", {"start": v(-3976.68, -1737.82) * mm, "end": v(-3945.09, -1798.2) * mm});
            skLineSegment(sketch, "E379", {"start": v(-3945.09, -1798.2) * mm, "end": v(-3909.97, -1856.8) * mm});
            skLineSegment(sketch, "E380", {"start": v(-3909.97, -1856.8) * mm, "end": v(-3871.15, -1913.92) * mm});
            skLineSegment(sketch, "E381", {"start": v(-3871.15, -1913.92) * mm, "end": v(-3828.45, -1969.92) * mm});
            skLineSegment(sketch, "E382", {"start": v(-3828.45, -1969.92) * mm, "end": v(-3781.7, -2025.13) * mm});
            skLineSegment(sketch, "E383", {"start": v(-3781.7, -2025.13) * mm, "end": v(-3730.73, -2079.87) * mm});
            skLineSegment(sketch, "E384", {"start": v(-3730.73, -2079.87) * mm, "end": v(-3716.24, -2086.1) * mm});
            skLineSegment(sketch, "E385", {"start": v(-3716.24, -2086.1) * mm, "end": v(-3701.43, -2091.78) * mm});
            skLineSegment(sketch, "E386", {"start": v(-3701.43, -2091.78) * mm, "end": v(-3686.31, -2096.89) * mm});
            skLineSegment(sketch, "E387", {"start": v(-3686.31, -2096.89) * mm, "end": v(-3670.9, -2101.43) * mm});
            skLineSegment(sketch, "E388", {"start": v(-3670.9, -2101.43) * mm, "end": v(-3655.22, -2105.42) * mm});
            skLineSegment(sketch, "E389", {"start": v(-3655.22, -2105.42) * mm, "end": v(-3639.28, -2108.84) * mm});
            skLineSegment(sketch, "E390", {"start": v(-3639.28, -2108.84) * mm, "end": v(-3623.1, -2111.71) * mm});
            skLineSegment(sketch, "E391", {"start": v(-3623.1, -2111.71) * mm, "end": v(-3606.7, -2114.03) * mm});
            skLineSegment(sketch, "E392", {"start": v(-3606.7, -2114.03) * mm, "end": v(-322.22, 1151.06) * mm});
            skLineSegment(sketch, "E393", {"start": v(-322.22, 1151.06) * mm, "end": v(-1524.18, 2345.9) * mm});
            skLineSegment(sketch, "E394", {"start": v(-1524.18, 2345.9) * mm, "end": v(-2036.53, 2858.6) * mm});
            skLineSegment(sketch, "E395", {"start": v(-2036.53, 2858.6) * mm, "end": v(-2563.21, 3393.3) * mm});
            skLineSegment(sketch, "E396", {"start": v(-2563.21, 3393.3) * mm, "end": v(-3096.86, 3944.04) * mm});
            skLineSegment(sketch, "E397", {"start": v(-3096.86, 3944.04) * mm, "end": v(-3630.16, 4504.84) * mm});
            skLineSegment(sketch, "E398", {"start": v(-3630.16, 4504.84) * mm, "end": v(-4155.74, 5069.73) * mm});
            skLineSegment(sketch, "E399", {"start": v(-4155.74, 5069.73) * mm, "end": v(-4666.28, 5632.74) * mm});
            skLineSegment(sketch, "E400", {"start": v(-4666.28, 5632.74) * mm, "end": v(-5154.43, 6187.9) * mm});
            skLineSegment(sketch, "E401", {"start": v(-5154.43, 6187.9) * mm, "end": v(-5612.84, 6729.26) * mm});
            skLineSegment(sketch, "E402", {"start": v(-5612.84, 6729.26) * mm, "end": v(-5626.05, 6742.4) * mm});
            skLineSegment(sketch, "E403", {"start": v(-5626.05, 6742.4) * mm, "end": v(-5625.63, 6742) * mm});
            skLineSegment(sketch, "E404", {"start": v(-5625.63, 6742) * mm, "end": v(-5624.54, 6741) * mm});
            skLineSegment(sketch, "E405", {"start": v(-5624.54, 6741) * mm, "end": v(-5622.99, 6739.57) * mm});
            skLineSegment(sketch, "E406", {"start": v(-5622.99, 6739.57) * mm, "end": v(-5621.21, 6737.93) * mm});
            skLineSegment(sketch, "E407", {"start": v(-5621.21, 6737.93) * mm, "end": v(-5619.43, 6736.3) * mm});
            skLineSegment(sketch, "E408", {"start": v(-5619.43, 6736.3) * mm, "end": v(-5617.88, 6734.87) * mm});
            skLineSegment(sketch, "E409", {"start": v(-5617.88, 6734.87) * mm, "end": v(-5616.79, 6733.86) * mm});
            skLineSegment(sketch, "E410", {"start": v(-5616.79, 6733.86) * mm, "end": v(-5616.37, 6733.48) * mm});
            skLineSegment(sketch, "E411", {"start": v(-5616.37, 6733.48) * mm, "end": v(-5616.55, 6733.7) * mm});
            skLineSegment(sketch, "E412", {"start": v(-5616.55, 6733.7) * mm, "end": v(-5617.03, 6734.27) * mm});
            skLineSegment(sketch, "E413", {"start": v(-5617.03, 6734.27) * mm, "end": v(-5617.71, 6735.08) * mm});
            skLineSegment(sketch, "E414", {"start": v(-5617.71, 6735.08) * mm, "end": v(-5618.5, 6736.02) * mm});
            skLineSegment(sketch, "E415", {"start": v(-5618.5, 6736.02) * mm, "end": v(-5619.27, 6736.95) * mm});
            skLineSegment(sketch, "E416", {"start": v(-5619.27, 6736.95) * mm, "end": v(-5619.95, 6737.76) * mm});
            skLineSegment(sketch, "E417", {"start": v(-5619.95, 6737.76) * mm, "end": v(-5620.43, 6738.34) * mm});
            skLineSegment(sketch, "E418", {"start": v(-5620.43, 6738.34) * mm, "end": v(-5620.61, 6738.56) * mm});
            skLineSegment(sketch, "E419", {"start": v(-5620.61, 6738.56) * mm, "end": v(-5074.1, 6284.57) * mm});
            skLineSegment(sketch, "E420", {"start": v(-5074.1, 6284.57) * mm, "end": v(-4514.32, 5799.8) * mm});
            skLineSegment(sketch, "E421", {"start": v(-4514.32, 5799.8) * mm, "end": v(-3947.1, 5291.81) * mm});
            skLineSegment(sketch, "E422", {"start": v(-3947.1, 5291.81) * mm, "end": v(-3378.3, 4768.17) * mm});
            skLineSegment(sketch, "E423", {"start": v(-3378.3, 4768.17) * mm, "end": v(-2813.73, 4236.43) * mm});
            skLineSegment(sketch, "E424", {"start": v(-2813.73, 4236.43) * mm, "end": v(-2259.28, 3704.17) * mm});
            skLineSegment(sketch, "E425", {"start": v(-2259.28, 3704.17) * mm, "end": v(-1720.76, 3178.95) * mm});
            skLineSegment(sketch, "E426", {"start": v(-1720.76, 3178.95) * mm, "end": v(-1204.04, 2668.33) * mm});
            skLineSegment(sketch, "E427", {"start": v(-1204.04, 2668.33) * mm, "end": v(0, 1471.38) * mm});
            skLineSegment(sketch, "E428", {"start": v(0, 1471.38) * mm, "end": v(1204.06, 2668.33) * mm});
            skLineSegment(sketch, "E429", {"start": v(1204.06, 2668.33) * mm, "end": v(1720.79, 3178.95) * mm});
            skLineSegment(sketch, "E430", {"start": v(1720.79, 3178.95) * mm, "end": v(2259.3, 3704.17) * mm});
            skLineSegment(sketch, "E431", {"start": v(2259.3, 3704.17) * mm, "end": v(2813.76, 4236.43) * mm});
            skLineSegment(sketch, "E432", {"start": v(2813.76, 4236.43) * mm, "end": v(3378.32, 4768.17) * mm});
            skLineSegment(sketch, "E433", {"start": v(3378.32, 4768.17) * mm, "end": v(3947.13, 5291.81) * mm});
            skLineSegment(sketch, "E434", {"start": v(3947.13, 5291.81) * mm, "end": v(4514.35, 5799.8) * mm});
            skLineSegment(sketch, "E435", {"start": v(4514.35, 5799.8) * mm, "end": v(5074.14, 6284.57) * mm});
            skLineSegment(sketch, "E436", {"start": v(5074.14, 6284.57) * mm, "end": v(5620.64, 6738.56) * mm});
            skLineSegment(sketch, "E437", {"start": v(5620.64, 6738.56) * mm, "end": v(5620.46, 6738.34) * mm});
            skLineSegment(sketch, "E438", {"start": v(5620.46, 6738.34) * mm, "end": v(5619.97, 6737.76) * mm});
            skLineSegment(sketch, "E439", {"start": v(5619.97, 6737.76) * mm, "end": v(5619.29, 6736.95) * mm});
            skLineSegment(sketch, "E440", {"start": v(5619.29, 6736.95) * mm, "end": v(5618.5, 6736.02) * mm});
            skLineSegment(sketch, "E441", {"start": v(5618.5, 6736.02) * mm, "end": v(5617.72, 6735.08) * mm});
            skLineSegment(sketch, "E442", {"start": v(5617.72, 6735.08) * mm, "end": v(5617.04, 6734.27) * mm});
            skLineSegment(sketch, "E443", {"start": v(5617.04, 6734.27) * mm, "end": v(5616.56, 6733.7) * mm});
            skLineSegment(sketch, "E444", {"start": v(5616.56, 6733.7) * mm, "end": v(5616.37, 6733.48) * mm});
            skLineSegment(sketch, "E445", {"start": v(5616.37, 6733.48) * mm, "end": v(5616.79, 6733.86) * mm});
            skLineSegment(sketch, "E446", {"start": v(5616.79, 6733.86) * mm, "end": v(5617.89, 6734.87) * mm});
            skLineSegment(sketch, "E447", {"start": v(5617.89, 6734.87) * mm, "end": v(5619.44, 6736.3) * mm});
            skLineSegment(sketch, "E448", {"start": v(5619.44, 6736.3) * mm, "end": v(5621.22, 6737.93) * mm});
            skLineSegment(sketch, "E449", {"start": v(5621.22, 6737.93) * mm, "end": v(5623, 6739.57) * mm});
            skLineSegment(sketch, "E450", {"start": v(5623, 6739.57) * mm, "end": v(5624.56, 6741) * mm});
            skLineSegment(sketch, "E451", {"start": v(5624.56, 6741) * mm, "end": v(5625.66, 6742) * mm});
            skLineSegment(sketch, "E452", {"start": v(5625.66, 6742) * mm, "end": v(5626.07, 6742.4) * mm});
            skLineSegment(sketch, "E453", {"start": v(5626.07, 6742.4) * mm, "end": v(5612.84, 6729.26) * mm});
            skLineSegment(sketch, "E454", {"start": v(5612.84, 6729.26) * mm, "end": v(5154.43, 6187.9) * mm});
            skLineSegment(sketch, "E455", {"start": v(5154.43, 6187.9) * mm, "end": v(4666.28, 5632.74) * mm});
            skLineSegment(sketch, "E456", {"start": v(4666.28, 5632.74) * mm, "end": v(4155.74, 5069.73) * mm});
            skLineSegment(sketch, "E457", {"start": v(4155.74, 5069.73) * mm, "end": v(3630.16, 4504.84) * mm});
            skLineSegment(sketch, "E458", {"start": v(3630.16, 4504.84) * mm, "end": v(3096.86, 3944.04) * mm});
            skLineSegment(sketch, "E459", {"start": v(3096.86, 3944.04) * mm, "end": v(2563.21, 3393.3) * mm});
            skLineSegment(sketch, "E460", {"start": v(2563.21, 3393.3) * mm, "end": v(2036.53, 2858.6) * mm});
            skLineSegment(sketch, "E461", {"start": v(2036.53, 2858.6) * mm, "end": v(1524.18, 2345.9) * mm});
            skLineSegment(sketch, "E462", {"start": v(1524.18, 2345.9) * mm, "end": v(322.22, 1151.06) * mm});
            skLineSegment(sketch, "E463", {"start": v(322.22, 1151.06) * mm, "end": v(3606.7, -2114.03) * mm});
            skLineSegment(sketch, "E464", {"start": v(-628.52, 7138.25) * mm, "end": v(-569.83, 7026.1) * mm});
            skLineSegment(sketch, "E465", {"start": v(-569.83, 7026.1) * mm, "end": v(-521.18, 6911.64) * mm});
            skLineSegment(sketch, "E466", {"start": v(-521.18, 6911.64) * mm, "end": v(-481.2, 6794.98) * mm});
            skLineSegment(sketch, "E467", {"start": v(-481.2, 6794.98) * mm, "end": v(-448.54, 6676.3) * mm});
            skLineSegment(sketch, "E468", {"start": v(-448.54, 6676.3) * mm, "end": v(-421.8, 6555.7) * mm});
            skLineSegment(sketch, "E469", {"start": v(-421.8, 6555.7) * mm, "end": v(-399.6, 6433.36) * mm});
            skLineSegment(sketch, "E470", {"start": v(-399.6, 6433.36) * mm, "end": v(-380.57, 6309.4) * mm});
            skLineSegment(sketch, "E471", {"start": v(-380.57, 6309.4) * mm, "end": v(-363.35, 6183.97) * mm});
            skLineSegment(sketch, "E472", {"start": v(-363.35, 6183.97) * mm, "end": v(-160.22, 6183.97) * mm});
            skLineSegment(sketch, "E473", {"start": v(-160.22, 6183.97) * mm, "end": v(-163.58, 6387.57) * mm});
            skLineSegment(sketch, "E474", {"start": v(-163.58, 6387.57) * mm, "end": v(-172.93, 6557.82) * mm});
            skLineSegment(sketch, "E475", {"start": v(-172.93, 6557.82) * mm, "end": v(-191.88, 6707.67) * mm});
            skLineSegment(sketch, "E476", {"start": v(-191.88, 6707.67) * mm, "end": v(-224.02, 6850.08) * mm});
            skLineSegment(sketch, "E477", {"start": v(-224.02, 6850.08) * mm, "end": v(-272.93, 6998) * mm});
            skLineSegment(sketch, "E478", {"start": v(-272.93, 6998) * mm, "end": v(-342.22, 7164.37) * mm});
            skLineSegment(sketch, "E479", {"start": v(-342.22, 7164.37) * mm, "end": v(-435.47, 7362.16) * mm});
            skLineSegment(sketch, "E480", {"start": v(-435.47, 7362.16) * mm, "end": v(-556.29, 7604.32) * mm});
            skLineSegment(sketch, "E481", {"start": v(-556.29, 7604.32) * mm, "end": v(-585.23, 7664.14) * mm});
            skLineSegment(sketch, "E482", {"start": v(-585.23, 7664.14) * mm, "end": v(-611.7, 7724.74) * mm});
            skLineSegment(sketch, "E483", {"start": v(-611.7, 7724.74) * mm, "end": v(-635.35, 7786.23) * mm});
            skLineSegment(sketch, "E484", {"start": v(-635.35, 7786.23) * mm, "end": v(-655.75, 7848.67) * mm});
            skLineSegment(sketch, "E485", {"start": v(-655.75, 7848.67) * mm, "end": v(-672.55, 7912.15) * mm});
            skLineSegment(sketch, "E486", {"start": v(-672.55, 7912.15) * mm, "end": v(-685.35, 7976.77) * mm});
            skLineSegment(sketch, "E487", {"start": v(-685.35, 7976.77) * mm, "end": v(-693.76, 8042.6) * mm});
            skLineSegment(sketch, "E488", {"start": v(-693.76, 8042.6) * mm, "end": v(-697.4, 8109.72) * mm});
            skLineSegment(sketch, "E489", {"start": v(-697.4, 8109.72) * mm, "end": v(-675.64, 8306.7) * mm});
            skLineSegment(sketch, "E490", {"start": v(-675.64, 8306.7) * mm, "end": v(-611.36, 8484.15) * mm});
            skLineSegment(sketch, "E491", {"start": v(-611.36, 8484.15) * mm, "end": v(-516.49, 8641.82) * mm});
            skLineSegment(sketch, "E492", {"start": v(-516.49, 8641.82) * mm, "end": v(-402.92, 8779.44) * mm});
            skLineSegment(sketch, "E493", {"start": v(-402.92, 8779.44) * mm, "end": v(-282.58, 8896.75) * mm});
            skLineSegment(sketch, "E494", {"start": v(-282.58, 8896.75) * mm, "end": v(-167.37, 8993.47) * mm});
            skLineSegment(sketch, "E495", {"start": v(-167.37, 8993.47) * mm, "end": v(-69.2, 9069.35) * mm});
            skLineSegment(sketch, "E496", {"start": v(-69.2, 9069.35) * mm, "end": v(0, 9124.12) * mm});
            skLineSegment(sketch, "E497", {"start": v(0, 9124.12) * mm, "end": v(69.2, 9069.35) * mm});
            skLineSegment(sketch, "E498", {"start": v(69.2, 9069.35) * mm, "end": v(167.37, 8993.47) * mm});
            skLineSegment(sketch, "E499", {"start": v(167.37, 8993.47) * mm, "end": v(282.58, 8896.75) * mm});
            skLineSegment(sketch, "E500", {"start": v(282.58, 8896.75) * mm, "end": v(402.92, 8779.44) * mm});
            skLineSegment(sketch, "E501", {"start": v(402.92, 8779.44) * mm, "end": v(516.49, 8641.82) * mm});
            skLineSegment(sketch, "E502", {"start": v(516.49, 8641.82) * mm, "end": v(611.36, 8484.15) * mm});
            skLineSegment(sketch, "E503", {"start": v(611.36, 8484.15) * mm, "end": v(675.64, 8306.7) * mm});
            skLineSegment(sketch, "E504", {"start": v(675.64, 8306.7) * mm, "end": v(697.4, 8109.72) * mm});
            skLineSegment(sketch, "E505", {"start": v(697.4, 8109.72) * mm, "end": v(693.76, 8042.6) * mm});
            skLineSegment(sketch, "E506", {"start": v(693.76, 8042.6) * mm, "end": v(685.35, 7976.77) * mm});
            skLineSegment(sketch, "E507", {"start": v(685.35, 7976.77) * mm, "end": v(672.56, 7912.15) * mm});
            skLineSegment(sketch, "E508", {"start": v(672.56, 7912.15) * mm, "end": v(655.76, 7848.67) * mm});
            skLineSegment(sketch, "E509", {"start": v(655.76, 7848.67) * mm, "end": v(635.36, 7786.23) * mm});
            skLineSegment(sketch, "E510", {"start": v(635.36, 7786.23) * mm, "end": v(611.72, 7724.74) * mm});
            skLineSegment(sketch, "E511", {"start": v(611.72, 7724.74) * mm, "end": v(585.23, 7664.14) * mm});
            skLineSegment(sketch, "E512", {"start": v(585.23, 7664.14) * mm, "end": v(556.29, 7604.32) * mm});
            skLineSegment(sketch, "E513", {"start": v(556.29, 7604.32) * mm, "end": v(435.47, 7362.16) * mm});
            skLineSegment(sketch, "E514", {"start": v(435.47, 7362.16) * mm, "end": v(342.22, 7164.37) * mm});
            skLineSegment(sketch, "E515", {"start": v(342.22, 7164.37) * mm, "end": v(272.93, 6998) * mm});
            skLineSegment(sketch, "E516", {"start": v(272.93, 6998) * mm, "end": v(224.02, 6850.08) * mm});
            skLineSegment(sketch, "E517", {"start": v(224.02, 6850.08) * mm, "end": v(191.88, 6707.67) * mm});
            skLineSegment(sketch, "E518", {"start": v(191.88, 6707.67) * mm, "end": v(172.93, 6557.82) * mm});
            skLineSegment(sketch, "E519", {"start": v(172.93, 6557.82) * mm, "end": v(163.58, 6387.57) * mm});
            skLineSegment(sketch, "E520", {"start": v(163.58, 6387.57) * mm, "end": v(160.22, 6183.97) * mm});
            skLineSegment(sketch, "E521", {"start": v(160.22, 6183.97) * mm, "end": v(363.35, 6183.97) * mm});
            skLineSegment(sketch, "E522", {"start": v(363.35, 6183.97) * mm, "end": v(380.57, 6309.4) * mm});
            skLineSegment(sketch, "E523", {"start": v(380.57, 6309.4) * mm, "end": v(399.6, 6433.36) * mm});
            skLineSegment(sketch, "E524", {"start": v(399.6, 6433.36) * mm, "end": v(421.8, 6555.7) * mm});
            skLineSegment(sketch, "E525", {"start": v(421.8, 6555.7) * mm, "end": v(448.54, 6676.3) * mm});
            skLineSegment(sketch, "E526", {"start": v(448.54, 6676.3) * mm, "end": v(481.2, 6794.98) * mm});
            skLineSegment(sketch, "E527", {"start": v(481.2, 6794.98) * mm, "end": v(521.18, 6911.64) * mm});
            skLineSegment(sketch, "E528", {"start": v(521.18, 6911.64) * mm, "end": v(569.83, 7026.1) * mm});
            skLineSegment(sketch, "E529", {"start": v(569.83, 7026.1) * mm, "end": v(628.52, 7138.25) * mm});
            skLineSegment(sketch, "E530", {"start": v(628.52, 7138.25) * mm, "end": v(893.22, 7465.35) * mm});
            skLineSegment(sketch, "E531", {"start": v(893.22, 7465.35) * mm, "end": v(1206.9, 7656.58) * mm});
            skLineSegment(sketch, "E532", {"start": v(1206.9, 7656.58) * mm, "end": v(1542.34, 7725.6) * mm});
            skLineSegment(sketch, "E533", {"start": v(1542.34, 7725.6) * mm, "end": v(1872.39, 7686.01) * mm});
            skLineSegment(sketch, "E534", {"start": v(1872.39, 7686.01) * mm, "end": v(2169.84, 7551.48) * mm});
            skLineSegment(sketch, "E535", {"start": v(2169.84, 7551.48) * mm, "end": v(2407.5, 7335.64) * mm});
            skLineSegment(sketch, "E536", {"start": v(2407.5, 7335.64) * mm, "end": v(2558.2, 7052.11) * mm});
            skLineSegment(sketch, "E537", {"start": v(2558.2, 7052.11) * mm, "end": v(2594.74, 6714.55) * mm});
            skLineSegment(sketch, "E538", {"start": v(2594.74, 6714.55) * mm, "end": v(2569.4, 6573.58) * mm});
            skLineSegment(sketch, "E539", {"start": v(2569.4, 6573.58) * mm, "end": v(2519.38, 6442.8) * mm});
            skLineSegment(sketch, "E540", {"start": v(2519.38, 6442.8) * mm, "end": v(2447.62, 6323.04) * mm});
            skLineSegment(sketch, "E541", {"start": v(2447.62, 6323.04) * mm, "end": v(2357.1, 6215.06) * mm});
            skLineSegment(sketch, "E542", {"start": v(2357.1, 6215.06) * mm, "end": v(2250.76, 6119.65) * mm});
            skLineSegment(sketch, "E543", {"start": v(2250.76, 6119.65) * mm, "end": v(2131.58, 6037.6) * mm});
            skLineSegment(sketch, "E544", {"start": v(2131.58, 6037.6) * mm, "end": v(2002.5, 5969.71) * mm});
            skLineSegment(sketch, "E545", {"start": v(2002.5, 5969.71) * mm, "end": v(1866.52, 5916.76) * mm});
            skLineSegment(sketch, "E546", {"start": v(1866.52, 5916.76) * mm, "end": v(1864.72, 5917.83) * mm});
            skLineSegment(sketch, "E547", {"start": v(1864.72, 5917.83) * mm, "end": v(1864.34, 5922.16) * mm});
            skLineSegment(sketch, "E548", {"start": v(1864.34, 5922.16) * mm, "end": v(1865.05, 5928.88) * mm});
            skLineSegment(sketch, "E549", {"start": v(1865.05, 5928.88) * mm, "end": v(1866.53, 5937.12) * mm});
            skLineSegment(sketch, "E550", {"start": v(1866.53, 5937.12) * mm, "end": v(1868.47, 5946) * mm});
            skLineSegment(sketch, "E551", {"start": v(1868.47, 5946) * mm, "end": v(1870.53, 5954.66) * mm});
            skLineSegment(sketch, "E552", {"start": v(1870.53, 5954.66) * mm, "end": v(1872.4, 5962.21) * mm});
            skLineSegment(sketch, "E553", {"start": v(1872.4, 5962.21) * mm, "end": v(1873.73, 5967.8) * mm});
            skLineSegment(sketch, "E554", {"start": v(1873.73, 5967.8) * mm, "end": v(1881.24, 6005.04) * mm});
            skLineSegment(sketch, "E555", {"start": v(1881.24, 6005.04) * mm, "end": v(1886.87, 6041.96) * mm});
            skLineSegment(sketch, "E556", {"start": v(1886.87, 6041.96) * mm, "end": v(1890.82, 6078.73) * mm});
            skLineSegment(sketch, "E557", {"start": v(1890.82, 6078.73) * mm, "end": v(1893.27, 6115.53) * mm});
            skLineSegment(sketch, "E558", {"start": v(1893.27, 6115.53) * mm, "end": v(1894.43, 6152.52) * mm});
            skLineSegment(sketch, "E559", {"start": v(1894.43, 6152.52) * mm, "end": v(1894.49, 6189.89) * mm});
            skLineSegment(sketch, "E560", {"start": v(1894.49, 6189.89) * mm, "end": v(1893.64, 6227.8) * mm});
            skLineSegment(sketch, "E561", {"start": v(1893.64, 6227.8) * mm, "end": v(1892.07, 6266.42) * mm});
            skLineSegment(sketch, "E562", {"start": v(1892.07, 6266.42) * mm, "end": v(1834.16, 6533.9) * mm});
            skLineSegment(sketch, "E563", {"start": v(1834.16, 6533.9) * mm, "end": v(1704.95, 6720.15) * mm});
            skLineSegment(sketch, "E564", {"start": v(1704.95, 6720.15) * mm, "end": v(1527.25, 6826.03) * mm});
            skLineSegment(sketch, "E565", {"start": v(1527.25, 6826.03) * mm, "end": v(1323.85, 6852.4) * mm});
            skLineSegment(sketch, "E566", {"start": v(1323.85, 6852.4) * mm, "end": v(1117.56, 6800.17) * mm});
            skLineSegment(sketch, "E567", {"start": v(1117.56, 6800.17) * mm, "end": v(931.17, 6670.17) * mm});
            skLineSegment(sketch, "E568", {"start": v(931.17, 6670.17) * mm, "end": v(787.47, 6463.29) * mm});
            skLineSegment(sketch, "E569", {"start": v(787.47, 6463.29) * mm, "end": v(709.27, 6180.4) * mm});
            skLineSegment(sketch, "E570", {"start": v(709.27, 6180.4) * mm, "end": v(817.6, 6180.4) * mm});
            skLineSegment(sketch, "E571", {"start": v(817.6, 6180.4) * mm, "end": v(875.3, 6174.57) * mm});
            skLineSegment(sketch, "E572", {"start": v(875.3, 6174.57) * mm, "end": v(929.04, 6157.9) * mm});
            skLineSegment(sketch, "E573", {"start": v(929.04, 6157.9) * mm, "end": v(977.67, 6131.5) * mm});
            skLineSegment(sketch, "E574", {"start": v(977.67, 6131.5) * mm, "end": v(1020.05, 6096.53) * mm});
            skLineSegment(sketch, "E575", {"start": v(1020.05, 6096.53) * mm, "end": v(1055, 6054.15) * mm});
            skLineSegment(sketch, "E576", {"start": v(1055, 6054.15) * mm, "end": v(1081.4, 6005.51) * mm});
            skLineSegment(sketch, "E577", {"start": v(1081.4, 6005.51) * mm, "end": v(1098.1, 5951.76) * mm});
            skLineSegment(sketch, "E578", {"start": v(1098.1, 5951.76) * mm, "end": v(1103.9, 5894.06) * mm});
            skLineSegment(sketch, "E579", {"start": v(1103.9, 5894.06) * mm, "end": v(1103.9, 5825.5) * mm});
            skLineSegment(sketch, "E580", {"start": v(1103.9, 5825.5) * mm, "end": v(1098.1, 5767.8) * mm});
            skLineSegment(sketch, "E581", {"start": v(1098.1, 5767.8) * mm, "end": v(1081.4, 5714.05) * mm});
            skLineSegment(sketch, "E582", {"start": v(1081.4, 5714.05) * mm, "end": v(1055, 5665.4) * mm});
            skLineSegment(sketch, "E583", {"start": v(1055, 5665.4) * mm, "end": v(1020.05, 5623.03) * mm});
            skLineSegment(sketch, "E584", {"start": v(1020.05, 5623.03) * mm, "end": v(977.67, 5588.07) * mm});
            skLineSegment(sketch, "E585", {"start": v(977.67, 5588.07) * mm, "end": v(929.04, 5561.67) * mm});
            skLineSegment(sketch, "E586", {"start": v(929.04, 5561.67) * mm, "end": v(875.3, 5544.99) * mm});
            skLineSegment(sketch, "E587", {"start": v(875.3, 5544.99) * mm, "end": v(817.6, 5539.17) * mm});
            skLineSegment(sketch, "E588", {"start": v(817.6, 5539.17) * mm, "end": v(695.66, 5539.17) * mm});
            skLineSegment(sketch, "E589", {"start": v(695.66, 5539.17) * mm, "end": v(732.71, 5363.74) * mm});
            skLineSegment(sketch, "E590", {"start": v(732.71, 5363.74) * mm, "end": v(807.02, 5233.84) * mm});
            skLineSegment(sketch, "E591", {"start": v(807.02, 5233.84) * mm, "end": v(907.93, 5146.93) * mm});
            skLineSegment(sketch, "E592", {"start": v(907.93, 5146.93) * mm, "end": v(1024.77, 5100.48) * mm});
            skLineSegment(sketch, "E593", {"start": v(1024.77, 5100.48) * mm, "end": v(1146.88, 5091.96) * mm});
            skLineSegment(sketch, "E594", {"start": v(1146.88, 5091.96) * mm, "end": v(1263.6, 5118.83) * mm});
            skLineSegment(sketch, "E595", {"start": v(1263.6, 5118.83) * mm, "end": v(1364.28, 5178.58) * mm});
            skLineSegment(sketch, "E596", {"start": v(1364.28, 5178.58) * mm, "end": v(1438.25, 5268.66) * mm});
            skLineSegment(sketch, "E597", {"start": v(1438.25, 5268.66) * mm, "end": v(1460.33, 5312.26) * mm});
            skLineSegment(sketch, "E598", {"start": v(1460.33, 5312.26) * mm, "end": v(1479.16, 5356.74) * mm});
            skLineSegment(sketch, "E599", {"start": v(1479.16, 5356.74) * mm, "end": v(1494.44, 5402.1) * mm});
            skLineSegment(sketch, "E600", {"start": v(1494.44, 5402.1) * mm, "end": v(1505.85, 5448.33) * mm});
            skLineSegment(sketch, "E601", {"start": v(1505.85, 5448.33) * mm, "end": v(1513.08, 5495.47) * mm});
            skLineSegment(sketch, "E602", {"start": v(1513.08, 5495.47) * mm, "end": v(1515.82, 5543.51) * mm});
            skLineSegment(sketch, "E603", {"start": v(1515.82, 5543.51) * mm, "end": v(1513.75, 5592.46) * mm});
            skLineSegment(sketch, "E604", {"start": v(1513.75, 5592.46) * mm, "end": v(1506.58, 5642.32) * mm});
            skLineSegment(sketch, "E605", {"start": v(1506.58, 5642.32) * mm, "end": v(1506.38, 5644.94) * mm});
            skLineSegment(sketch, "E606", {"start": v(1506.38, 5644.94) * mm, "end": v(1506.83, 5647.25) * mm});
            skLineSegment(sketch, "E607", {"start": v(1506.83, 5647.25) * mm, "end": v(1507.82, 5649.17) * mm});
            skLineSegment(sketch, "E608", {"start": v(1507.82, 5649.17) * mm, "end": v(1509.28, 5650.61) * mm});
            skLineSegment(sketch, "E609", {"start": v(1509.28, 5650.61) * mm, "end": v(1511.11, 5651.52) * mm});
            skLineSegment(sketch, "E610", {"start": v(1511.11, 5651.52) * mm, "end": v(1513.23, 5651.8) * mm});
            skLineSegment(sketch, "E611", {"start": v(1513.23, 5651.8) * mm, "end": v(1515.55, 5651.37) * mm});
            skLineSegment(sketch, "E612", {"start": v(1515.55, 5651.37) * mm, "end": v(1517.98, 5650.17) * mm});
            skLineSegment(sketch, "E613", {"start": v(1517.98, 5650.17) * mm, "end": v(1689.61, 5509.94) * mm});
            skLineSegment(sketch, "E614", {"start": v(1689.61, 5509.94) * mm, "end": v(1816.3, 5350.24) * mm});
            skLineSegment(sketch, "E615", {"start": v(1816.3, 5350.24) * mm, "end": v(1896.9, 5178.52) * mm});
            skLineSegment(sketch, "E616", {"start": v(1896.9, 5178.52) * mm, "end": v(1930.26, 5002.23) * mm});
            skLineSegment(sketch, "E617", {"start": v(1930.26, 5002.23) * mm, "end": v(1915.25, 4828.82) * mm});
            skLineSegment(sketch, "E618", {"start": v(1915.25, 4828.82) * mm, "end": v(1850.74, 4665.76) * mm});
            skLineSegment(sketch, "E619", {"start": v(1850.74, 4665.76) * mm, "end": v(1735.58, 4520.5) * mm});
            skLineSegment(sketch, "E620", {"start": v(1735.58, 4520.5) * mm, "end": v(1568.63, 4400.49) * mm});
            skLineSegment(sketch, "E621", {"start": v(1568.63, 4400.49) * mm, "end": v(1497.6, 4369.18) * mm});
            skLineSegment(sketch, "E622", {"start": v(1497.6, 4369.18) * mm, "end": v(1420.9, 4348.34) * mm});
            skLineSegment(sketch, "E623", {"start": v(1420.9, 4348.34) * mm, "end": v(1340.39, 4337.55) * mm});
            skLineSegment(sketch, "E624", {"start": v(1340.39, 4337.55) * mm, "end": v(1257.96, 4336.37) * mm});
            skLineSegment(sketch, "E625", {"start": v(1257.96, 4336.37) * mm, "end": v(1175.5, 4344.37) * mm});
            skLineSegment(sketch, "E626", {"start": v(1175.5, 4344.37) * mm, "end": v(1094.88, 4361.14) * mm});
            skLineSegment(sketch, "E627", {"start": v(1094.88, 4361.14) * mm, "end": v(1017.98, 4386.25) * mm});
            skLineSegment(sketch, "E628", {"start": v(1017.98, 4386.25) * mm, "end": v(946.68, 4419.26) * mm});
            skLineSegment(sketch, "E629", {"start": v(946.68, 4419.26) * mm, "end": v(816.13, 4508.01) * mm});
            skLineSegment(sketch, "E630", {"start": v(816.13, 4508.01) * mm, "end": v(703.16, 4620.05) * mm});
            skLineSegment(sketch, "E631", {"start": v(703.16, 4620.05) * mm, "end": v(607.3, 4751.05) * mm});
            skLineSegment(sketch, "E632", {"start": v(607.3, 4751.05) * mm, "end": v(528.09, 4896.68) * mm});
            skLineSegment(sketch, "E633", {"start": v(528.09, 4896.68) * mm, "end": v(465.06, 5052.63) * mm});
            skLineSegment(sketch, "E634", {"start": v(465.06, 5052.63) * mm, "end": v(417.75, 5214.57) * mm});
            skLineSegment(sketch, "E635", {"start": v(417.75, 5214.57) * mm, "end": v(385.7, 5378.2) * mm});
            skLineSegment(sketch, "E636", {"start": v(385.7, 5378.2) * mm, "end": v(368.45, 5539.17) * mm});
            skLineSegment(sketch, "E637", {"start": v(368.45, 5539.17) * mm, "end": v(159.9, 5539.17) * mm});
            skLineSegment(sketch, "E638", {"start": v(159.9, 5539.17) * mm, "end": v(170.37, 5253) * mm});
            skLineSegment(sketch, "E639", {"start": v(170.37, 5253) * mm, "end": v(217.12, 5014.9) * mm});
            skLineSegment(sketch, "E640", {"start": v(217.12, 5014.9) * mm, "end": v(286.83, 4813.77) * mm});
            skLineSegment(sketch, "E641", {"start": v(286.83, 4813.77) * mm, "end": v(366.17, 4638.5) * mm});
            skLineSegment(sketch, "E642", {"start": v(366.17, 4638.5) * mm, "end": v(441.82, 4478.02) * mm});
            skLineSegment(sketch, "E643", {"start": v(441.82, 4478.02) * mm, "end": v(500.46, 4321.2) * mm});
            skLineSegment(sketch, "E644", {"start": v(500.46, 4321.2) * mm, "end": v(528.78, 4156.96) * mm});
            skLineSegment(sketch, "E645", {"start": v(528.78, 4156.96) * mm, "end": v(513.46, 3974.2) * mm});
            skLineSegment(sketch, "E646", {"start": v(513.46, 3974.2) * mm, "end": v(483.47, 3875.38) * mm});
            skLineSegment(sketch, "E647", {"start": v(483.47, 3875.38) * mm, "end": v(439.35, 3787) * mm});
            skLineSegment(sketch, "E648", {"start": v(439.35, 3787) * mm, "end": v(383.27, 3707.86) * mm});
            skLineSegment(sketch, "E649", {"start": v(383.27, 3707.86) * mm, "end": v(317.42, 3636.72) * mm});
            skLineSegment(sketch, "E650", {"start": v(317.42, 3636.72) * mm, "end": v(244, 3572.36) * mm});
            skLineSegment(sketch, "E651", {"start": v(244, 3572.36) * mm, "end": v(165.15, 3513.56) * mm});
            skLineSegment(sketch, "E652", {"start": v(165.15, 3513.56) * mm, "end": v(83.1, 3459.1) * mm});
            skLineSegment(sketch, "E653", {"start": v(83.1, 3459.1) * mm, "end": v(0, 3407.75) * mm});
            skLineSegment(sketch, "E654", {"start": v(0, 3407.75) * mm, "end": v(-83.1, 3459.1) * mm});
            skLineSegment(sketch, "E655", {"start": v(-83.1, 3459.1) * mm, "end": v(-165.15, 3513.56) * mm});
            skLineSegment(sketch, "E656", {"start": v(-165.15, 3513.56) * mm, "end": v(-244, 3572.36) * mm});
            skLineSegment(sketch, "E657", {"start": v(-244, 3572.36) * mm, "end": v(-317.42, 3636.72) * mm});
            skLineSegment(sketch, "E658", {"start": v(-317.42, 3636.72) * mm, "end": v(-383.27, 3707.86) * mm});
            skLineSegment(sketch, "E659", {"start": v(-383.27, 3707.86) * mm, "end": v(-439.35, 3787) * mm});
            skLineSegment(sketch, "E660", {"start": v(-439.35, 3787) * mm, "end": v(-483.47, 3875.38) * mm});
            skLineSegment(sketch, "E661", {"start": v(-483.47, 3875.38) * mm, "end": v(-513.46, 3974.2) * mm});
            skLineSegment(sketch, "E662", {"start": v(-513.46, 3974.2) * mm, "end": v(-528.78, 4156.96) * mm});
            skLineSegment(sketch, "E663", {"start": v(-528.78, 4156.96) * mm, "end": v(-500.46, 4321.2) * mm});
            skLineSegment(sketch, "E664", {"start": v(-500.46, 4321.2) * mm, "end": v(-441.82, 4478.02) * mm});
            skLineSegment(sketch, "E665", {"start": v(-441.82, 4478.02) * mm, "end": v(-366.17, 4638.5) * mm});
            skLineSegment(sketch, "E666", {"start": v(-366.17, 4638.5) * mm, "end": v(-286.83, 4813.77) * mm});
            skLineSegment(sketch, "E667", {"start": v(-286.83, 4813.77) * mm, "end": v(-217.12, 5014.9) * mm});
            skLineSegment(sketch, "E668", {"start": v(-217.12, 5014.9) * mm, "end": v(-170.37, 5253) * mm});
            skLineSegment(sketch, "E669", {"start": v(-170.37, 5253) * mm, "end": v(-159.9, 5539.17) * mm});
            skLineSegment(sketch, "E670", {"start": v(-159.9, 5539.17) * mm, "end": v(-368.45, 5539.17) * mm});
            skLineSegment(sketch, "E671", {"start": v(-368.45, 5539.17) * mm, "end": v(-385.7, 5378.2) * mm});
            skLineSegment(sketch, "E672", {"start": v(-385.7, 5378.2) * mm, "end": v(-417.74, 5214.57) * mm});
            skLineSegment(sketch, "E673", {"start": v(-417.74, 5214.57) * mm, "end": v(-465.05, 5052.63) * mm});
            skLineSegment(sketch, "E674", {"start": v(-465.05, 5052.63) * mm, "end": v(-528.07, 4896.68) * mm});
            skLineSegment(sketch, "E675", {"start": v(-528.07, 4896.68) * mm, "end": v(-607.28, 4751.05) * mm});
            skLineSegment(sketch, "E676", {"start": v(-607.28, 4751.05) * mm, "end": v(-703.14, 4620.05) * mm});
            skLineSegment(sketch, "E677", {"start": v(-703.14, 4620.05) * mm, "end": v(-816.11, 4508.01) * mm});
            skLineSegment(sketch, "E678", {"start": v(-816.11, 4508.01) * mm, "end": v(-946.66, 4419.26) * mm});
            skLineSegment(sketch, "E679", {"start": v(-946.66, 4419.26) * mm, "end": v(-1017.96, 4386.25) * mm});
            skLineSegment(sketch, "E680", {"start": v(-1017.96, 4386.25) * mm, "end": v(-1094.87, 4361.14) * mm});
            skLineSegment(sketch, "E681", {"start": v(-1094.87, 4361.14) * mm, "end": v(-1175.5, 4344.37) * mm});
            skLineSegment(sketch, "E682", {"start": v(-1175.5, 4344.37) * mm, "end": v(-1257.96, 4336.37) * mm});
            skLineSegment(sketch, "E683", {"start": v(-1257.96, 4336.37) * mm, "end": v(-1340.38, 4337.55) * mm});
            skLineSegment(sketch, "E684", {"start": v(-1340.38, 4337.55) * mm, "end": v(-1420.9, 4348.34) * mm});
            skLineSegment(sketch, "E685", {"start": v(-1420.9, 4348.34) * mm, "end": v(-1497.6, 4369.18) * mm});
            skLineSegment(sketch, "E686", {"start": v(-1497.6, 4369.18) * mm, "end": v(-1568.63, 4400.49) * mm});
            skLineSegment(sketch, "E687", {"start": v(-1568.63, 4400.49) * mm, "end": v(-1735.58, 4520.5) * mm});
            skLineSegment(sketch, "E688", {"start": v(-1735.58, 4520.5) * mm, "end": v(-1850.74, 4665.76) * mm});
            skLineSegment(sketch, "E689", {"start": v(-1850.74, 4665.76) * mm, "end": v(-1915.25, 4828.82) * mm});
            skLineSegment(sketch, "E690", {"start": v(-1915.25, 4828.82) * mm, "end": v(-1930.26, 5002.23) * mm});
            skLineSegment(sketch, "E691", {"start": v(-1930.26, 5002.23) * mm, "end": v(-1896.9, 5178.52) * mm});
            skLineSegment(sketch, "E692", {"start": v(-1896.9, 5178.52) * mm, "end": v(-1816.3, 5350.24) * mm});
            skLineSegment(sketch, "E693", {"start": v(-1816.3, 5350.24) * mm, "end": v(-1689.61, 5509.94) * mm});
            skLineSegment(sketch, "E694", {"start": v(-1689.61, 5509.94) * mm, "end": v(-1517.98, 5650.17) * mm});
            skLineSegment(sketch, "E695", {"start": v(-1517.98, 5650.17) * mm, "end": v(-1515.54, 5651.37) * mm});
            skLineSegment(sketch, "E696", {"start": v(-1515.54, 5651.37) * mm, "end": v(-1513.22, 5651.8) * mm});
            skLineSegment(sketch, "E697", {"start": v(-1513.22, 5651.8) * mm, "end": v(-1511.1, 5651.52) * mm});
            skLineSegment(sketch, "E698", {"start": v(-1511.1, 5651.52) * mm, "end": v(-1509.27, 5650.61) * mm});
            skLineSegment(sketch, "E699", {"start": v(-1509.27, 5650.61) * mm, "end": v(-1507.81, 5649.17) * mm});
            skLineSegment(sketch, "E700", {"start": v(-1507.81, 5649.17) * mm, "end": v(-1506.82, 5647.25) * mm});
            skLineSegment(sketch, "E701", {"start": v(-1506.82, 5647.25) * mm, "end": v(-1506.38, 5644.94) * mm});
            skLineSegment(sketch, "E702", {"start": v(-1506.38, 5644.94) * mm, "end": v(-1506.58, 5642.32) * mm});
            skLineSegment(sketch, "E703", {"start": v(-1506.58, 5642.32) * mm, "end": v(-1513.75, 5592.46) * mm});
            skLineSegment(sketch, "E704", {"start": v(-1513.75, 5592.46) * mm, "end": v(-1515.82, 5543.51) * mm});
            skLineSegment(sketch, "E705", {"start": v(-1515.82, 5543.51) * mm, "end": v(-1513.08, 5495.47) * mm});
            skLineSegment(sketch, "E706", {"start": v(-1513.08, 5495.47) * mm, "end": v(-1505.85, 5448.33) * mm});
            skLineSegment(sketch, "E707", {"start": v(-1505.85, 5448.33) * mm, "end": v(-1494.44, 5402.1) * mm});
            skLineSegment(sketch, "E708", {"start": v(-1494.44, 5402.1) * mm, "end": v(-1479.16, 5356.74) * mm});
            skLineSegment(sketch, "E709", {"start": v(-1479.16, 5356.74) * mm, "end": v(-1460.33, 5312.26) * mm});
            skLineSegment(sketch, "E710", {"start": v(-1460.33, 5312.26) * mm, "end": v(-1438.25, 5268.66) * mm});
            skLineSegment(sketch, "E711", {"start": v(-1438.25, 5268.66) * mm, "end": v(-1364.28, 5178.58) * mm});
            skLineSegment(sketch, "E712", {"start": v(-1364.28, 5178.58) * mm, "end": v(-1263.6, 5118.83) * mm});
            skLineSegment(sketch, "E713", {"start": v(-1263.6, 5118.83) * mm, "end": v(-1146.88, 5091.96) * mm});
            skLineSegment(sketch, "E714", {"start": v(-1146.88, 5091.96) * mm, "end": v(-1024.77, 5100.48) * mm});
            skLineSegment(sketch, "E715", {"start": v(-1024.77, 5100.48) * mm, "end": v(-907.93, 5146.93) * mm});
            skLineSegment(sketch, "E716", {"start": v(-907.93, 5146.93) * mm, "end": v(-807.02, 5233.84) * mm});
            skLineSegment(sketch, "E717", {"start": v(-807.02, 5233.84) * mm, "end": v(-732.71, 5363.74) * mm});
            skLineSegment(sketch, "E718", {"start": v(-732.71, 5363.74) * mm, "end": v(-695.66, 5539.17) * mm});
            skLineSegment(sketch, "E719", {"start": v(-695.66, 5539.17) * mm, "end": v(-817.58, 5539.17) * mm});
            skLineSegment(sketch, "E720", {"start": v(-817.58, 5539.17) * mm, "end": v(-875.28, 5544.99) * mm});
            skLineSegment(sketch, "E721", {"start": v(-875.28, 5544.99) * mm, "end": v(-929.03, 5561.67) * mm});
            skLineSegment(sketch, "E722", {"start": v(-929.03, 5561.67) * mm, "end": v(-977.67, 5588.07) * mm});
            skLineSegment(sketch, "E723", {"start": v(-977.67, 5588.07) * mm, "end": v(-1020.04, 5623.03) * mm});
            skLineSegment(sketch, "E724", {"start": v(-1020.04, 5623.03) * mm, "end": v(-1055, 5665.4) * mm});
            skLineSegment(sketch, "E725", {"start": v(-1055, 5665.4) * mm, "end": v(-1081.4, 5714.05) * mm});
            skLineSegment(sketch, "E726", {"start": v(-1081.4, 5714.05) * mm, "end": v(-1098.1, 5767.8) * mm});
            skLineSegment(sketch, "E727", {"start": v(-1098.1, 5767.8) * mm, "end": v(-1103.9, 5825.5) * mm});
            skLineSegment(sketch, "E728", {"start": v(-1103.9, 5825.5) * mm, "end": v(-1103.9, 5894.06) * mm});
            skLineSegment(sketch, "E729", {"start": v(-1103.9, 5894.06) * mm, "end": v(-1098.1, 5951.76) * mm});
            skLineSegment(sketch, "E730", {"start": v(-1098.1, 5951.76) * mm, "end": v(-1081.4, 6005.51) * mm});
            skLineSegment(sketch, "E731", {"start": v(-1081.4, 6005.51) * mm, "end": v(-1055, 6054.15) * mm});
            skLineSegment(sketch, "E732", {"start": v(-1055, 6054.15) * mm, "end": v(-1020.04, 6096.53) * mm});
            skLineSegment(sketch, "E733", {"start": v(-1020.04, 6096.53) * mm, "end": v(-977.67, 6131.5) * mm});
            skLineSegment(sketch, "E734", {"start": v(-977.67, 6131.5) * mm, "end": v(-929.03, 6157.9) * mm});
            skLineSegment(sketch, "E735", {"start": v(-929.03, 6157.9) * mm, "end": v(-875.28, 6174.57) * mm});
            skLineSegment(sketch, "E736", {"start": v(-875.28, 6174.57) * mm, "end": v(-817.58, 6180.4) * mm});
            skLineSegment(sketch, "E737", {"start": v(-817.58, 6180.4) * mm, "end": v(-709.27, 6180.4) * mm});
            skLineSegment(sketch, "E738", {"start": v(-709.27, 6180.4) * mm, "end": v(-787.47, 6463.29) * mm});
            skLineSegment(sketch, "E739", {"start": v(-787.47, 6463.29) * mm, "end": v(-931.17, 6670.17) * mm});
            skLineSegment(sketch, "E740", {"start": v(-931.17, 6670.17) * mm, "end": v(-1117.56, 6800.17) * mm});
            skLineSegment(sketch, "E741", {"start": v(-1117.56, 6800.17) * mm, "end": v(-1323.85, 6852.4) * mm});
            skLineSegment(sketch, "E742", {"start": v(-1323.85, 6852.4) * mm, "end": v(-1527.25, 6826.03) * mm});
            skLineSegment(sketch, "E743", {"start": v(-1527.25, 6826.03) * mm, "end": v(-1704.95, 6720.15) * mm});
            skLineSegment(sketch, "E744", {"start": v(-1704.95, 6720.15) * mm, "end": v(-1834.16, 6533.9) * mm});
            skLineSegment(sketch, "E745", {"start": v(-1834.16, 6533.9) * mm, "end": v(-1892.07, 6266.42) * mm});
            skLineSegment(sketch, "E746", {"start": v(-1892.07, 6266.42) * mm, "end": v(-1893.64, 6227.8) * mm});
            skLineSegment(sketch, "E747", {"start": v(-1893.64, 6227.8) * mm, "end": v(-1894.49, 6189.89) * mm});
            skLineSegment(sketch, "E748", {"start": v(-1894.49, 6189.89) * mm, "end": v(-1894.43, 6152.52) * mm});
            skLineSegment(sketch, "E749", {"start": v(-1894.43, 6152.52) * mm, "end": v(-1893.27, 6115.53) * mm});
            skLineSegment(sketch, "E750", {"start": v(-1893.27, 6115.53) * mm, "end": v(-1890.82, 6078.73) * mm});
            skLineSegment(sketch, "E751", {"start": v(-1890.82, 6078.73) * mm, "end": v(-1886.87, 6041.96) * mm});
            skLineSegment(sketch, "E752", {"start": v(-1886.87, 6041.96) * mm, "end": v(-1881.24, 6005.04) * mm});
            skLineSegment(sketch, "E753", {"start": v(-1881.24, 6005.04) * mm, "end": v(-1873.73, 5967.8) * mm});
            skLineSegment(sketch, "E754", {"start": v(-1873.73, 5967.8) * mm, "end": v(-1872.4, 5962.21) * mm});
            skLineSegment(sketch, "E755", {"start": v(-1872.4, 5962.21) * mm, "end": v(-1870.53, 5954.66) * mm});
            skLineSegment(sketch, "E756", {"start": v(-1870.53, 5954.66) * mm, "end": v(-1868.47, 5946) * mm});
            skLineSegment(sketch, "E757", {"start": v(-1868.47, 5946) * mm, "end": v(-1866.53, 5937.12) * mm});
            skLineSegment(sketch, "E758", {"start": v(-1866.53, 5937.12) * mm, "end": v(-1865.05, 5928.88) * mm});
            skLineSegment(sketch, "E759", {"start": v(-1865.05, 5928.88) * mm, "end": v(-1864.34, 5922.16) * mm});
            skLineSegment(sketch, "E760", {"start": v(-1864.34, 5922.16) * mm, "end": v(-1864.72, 5917.83) * mm});
            skLineSegment(sketch, "E761", {"start": v(-1864.72, 5917.83) * mm, "end": v(-1866.52, 5916.76) * mm});
            skLineSegment(sketch, "E762", {"start": v(-1866.52, 5916.76) * mm, "end": v(-2002.5, 5969.71) * mm});
            skLineSegment(sketch, "E763", {"start": v(-2002.5, 5969.71) * mm, "end": v(-2131.56, 6037.6) * mm});
            skLineSegment(sketch, "E764", {"start": v(-2131.56, 6037.6) * mm, "end": v(-2250.74, 6119.65) * mm});
            skLineSegment(sketch, "E765", {"start": v(-2250.74, 6119.65) * mm, "end": v(-2357.08, 6215.06) * mm});
            skLineSegment(sketch, "E766", {"start": v(-2357.08, 6215.06) * mm, "end": v(-2447.6, 6323.04) * mm});
            skLineSegment(sketch, "E767", {"start": v(-2447.6, 6323.04) * mm, "end": v(-2519.36, 6442.8) * mm});
            skLineSegment(sketch, "E768", {"start": v(-2519.36, 6442.8) * mm, "end": v(-2569.38, 6573.58) * mm});
            skLineSegment(sketch, "E769", {"start": v(-2569.38, 6573.58) * mm, "end": v(-2594.71, 6714.55) * mm});
            skLineSegment(sketch, "E770", {"start": v(-2594.71, 6714.55) * mm, "end": v(-2558.18, 7052.11) * mm});
            skLineSegment(sketch, "E771", {"start": v(-2558.18, 7052.11) * mm, "end": v(-2407.5, 7335.64) * mm});
            skLineSegment(sketch, "E772", {"start": v(-2407.5, 7335.64) * mm, "end": v(-2169.83, 7551.48) * mm});
            skLineSegment(sketch, "E773", {"start": v(-2169.83, 7551.48) * mm, "end": v(-1872.38, 7686.01) * mm});
            skLineSegment(sketch, "E774", {"start": v(-1872.38, 7686.01) * mm, "end": v(-1542.34, 7725.6) * mm});
            skLineSegment(sketch, "E775", {"start": v(-1542.34, 7725.6) * mm, "end": v(-1206.9, 7656.58) * mm});
            skLineSegment(sketch, "E776", {"start": v(-1206.9, 7656.58) * mm, "end": v(-893.22, 7465.35) * mm});
            skLineSegment(sketch, "E777", {"start": v(-893.22, 7465.35) * mm, "end": v(-628.52, 7138.25) * mm});
            skLineSegment(sketch, "E778", {"start": v(8516.95, 8076.12) * mm, "end": v(7886.24, 8206.58) * mm});
            skLineSegment(sketch, "E779", {"start": v(7886.24, 8206.58) * mm, "end": v(7335.12, 8390.4) * mm});
            skLineSegment(sketch, "E780", {"start": v(7335.12, 8390.4) * mm, "end": v(6861, 8629.9) * mm});
            skLineSegment(sketch, "E781", {"start": v(6861, 8629.9) * mm, "end": v(6461.28, 8927.45) * mm});
            skLineSegment(sketch, "E782", {"start": v(6461.28, 8927.45) * mm, "end": v(6133.36, 9285.35) * mm});
            skLineSegment(sketch, "E783", {"start": v(6133.36, 9285.35) * mm, "end": v(5874.65, 9705.96) * mm});
            skLineSegment(sketch, "E784", {"start": v(5874.65, 9705.96) * mm, "end": v(5682.55, 10191.61) * mm});
            skLineSegment(sketch, "E785", {"start": v(5682.55, 10191.61) * mm, "end": v(5554.47, 10744.64) * mm});
            skLineSegment(sketch, "E786", {"start": v(5554.47, 10744.64) * mm, "end": v(5496.23, 11097.65) * mm});
            skLineSegment(sketch, "E787", {"start": v(5496.23, 11097.65) * mm, "end": v(-5496.05, 11097.65) * mm});
            skLineSegment(sketch, "E788", {"start": v(-5496.05, 11097.65) * mm, "end": v(-5554.3, 10744.64) * mm});
            skLineSegment(sketch, "E789", {"start": v(-5554.3, 10744.64) * mm, "end": v(-5682.36, 10191.6) * mm});
            skLineSegment(sketch, "E790", {"start": v(-5682.36, 10191.6) * mm, "end": v(-5874.46, 9705.93) * mm});
            skLineSegment(sketch, "E791", {"start": v(-5874.46, 9705.93) * mm, "end": v(-6133.17, 9285.31) * mm});
            skLineSegment(sketch, "E792", {"start": v(-6133.17, 9285.31) * mm, "end": v(-6461.1, 8927.4) * mm});
            skLineSegment(sketch, "E793", {"start": v(-6461.1, 8927.4) * mm, "end": v(-6860.86, 8629.87) * mm});
            skLineSegment(sketch, "E794", {"start": v(-6860.86, 8629.87) * mm, "end": v(-7335.01, 8390.37) * mm});
            skLineSegment(sketch, "E795", {"start": v(-7335.01, 8390.37) * mm, "end": v(-7886.17, 8206.57) * mm});
            skLineSegment(sketch, "E796", {"start": v(-7886.17, 8206.57) * mm, "end": v(-8516.92, 8076.12) * mm});
            skLineSegment(sketch, "E797", {"start": v(-8516.92, 8076.12) * mm, "end": v(-8881.7, 8019.28) * mm});
            skLineSegment(sketch, "E798", {"start": v(-8881.7, 8019.28) * mm, "end": v(-8873.62, 7650.26) * mm});
            skLineSegment(sketch, "E799", {"start": v(-8873.62, 7650.26) * mm, "end": v(-8816.76, 5895.27) * mm});
            skLineSegment(sketch, "E800", {"start": v(-8816.76, 5895.27) * mm, "end": v(-8725.31, 4302.1) * mm});
            skLineSegment(sketch, "E801", {"start": v(-8725.31, 4302.1) * mm, "end": v(-8597.44, 2858.47) * mm});
            skLineSegment(sketch, "E802", {"start": v(-8597.44, 2858.47) * mm, "end": v(-8431.3, 1552.1) * mm});
            skLineSegment(sketch, "E803", {"start": v(-8431.3, 1552.1) * mm, "end": v(-8225.05, 370.69) * mm});
            skLineSegment(sketch, "E804", {"start": v(-8225.05, 370.69) * mm, "end": v(-7976.86, -698.03) * mm});
            skLineSegment(sketch, "E805", {"start": v(-7976.86, -698.03) * mm, "end": v(-7684.88, -1666.36) * mm});
            skLineSegment(sketch, "E806", {"start": v(-7684.88, -1666.36) * mm, "end": v(-7347.28, -2546.57) * mm});
            skLineSegment(sketch, "E807", {"start": v(-7347.28, -2546.57) * mm, "end": v(-6977.33, -3324.62) * mm});
            skLineSegment(sketch, "E808", {"start": v(-6977.33, -3324.62) * mm, "end": v(-6568.55, -4035.73) * mm});
            skLineSegment(sketch, "E809", {"start": v(-6568.55, -4035.73) * mm, "end": v(-6119.6, -4696.1) * mm});
            skLineSegment(sketch, "E810", {"start": v(-6119.6, -4696.1) * mm, "end": v(-5629.16, -5321.94) * mm});
            skLineSegment(sketch, "E811", {"start": v(-5629.16, -5321.94) * mm, "end": v(-5095.91, -5929.46) * mm});
            skLineSegment(sketch, "E812", {"start": v(-5095.91, -5929.46) * mm, "end": v(-4518.53, -6534.86) * mm});
            skLineSegment(sketch, "E813", {"start": v(-4518.53, -6534.86) * mm, "end": v(-3895.7, -7154.35) * mm});
            skLineSegment(sketch, "E814", {"start": v(-3895.7, -7154.35) * mm, "end": v(-3226.08, -7804.14) * mm});
            skLineSegment(sketch, "E815", {"start": v(-3226.08, -7804.14) * mm, "end": v(-2898.62, -8120.95) * mm});
            skLineSegment(sketch, "E816", {"start": v(-2898.62, -8120.95) * mm, "end": v(-2560.48, -8449.68) * mm});
            skLineSegment(sketch, "E817", {"start": v(-2560.48, -8449.68) * mm, "end": v(-2211.72, -8791.87) * mm});
            skLineSegment(sketch, "E818", {"start": v(-2211.72, -8791.87) * mm, "end": v(-1852.4, -9149.03) * mm});
            skLineSegment(sketch, "E819", {"start": v(-1852.4, -9149.03) * mm, "end": v(-1482.6, -9522.7) * mm});
            skLineSegment(sketch, "E820", {"start": v(-1482.6, -9522.7) * mm, "end": v(-1102.37, -9914.4) * mm});
            skLineSegment(sketch, "E821", {"start": v(-1102.37, -9914.4) * mm, "end": v(-711.77, -10325.67) * mm});
            skLineSegment(sketch, "E822", {"start": v(-711.77, -10325.67) * mm, "end": v(-310.87, -10758.03) * mm});
            skLineSegment(sketch, "E823", {"start": v(-310.87, -10758.03) * mm, "end": v(0.13, -11097.65) * mm});
            skLineSegment(sketch, "E824", {"start": v(0.13, -11097.65) * mm, "end": v(311.12, -10758.03) * mm});
            skLineSegment(sketch, "E825", {"start": v(311.12, -10758.03) * mm, "end": v(712, -10325.7) * mm});
            skLineSegment(sketch, "E826", {"start": v(712, -10325.7) * mm, "end": v(1102.58, -9914.45) * mm});
            skLineSegment(sketch, "E827", {"start": v(1102.58, -9914.45) * mm, "end": v(1482.78, -9522.78) * mm});
            skLineSegment(sketch, "E828", {"start": v(1482.78, -9522.78) * mm, "end": v(1852.56, -9149.14) * mm});
            skLineSegment(sketch, "E829", {"start": v(1852.56, -9149.14) * mm, "end": v(2211.83, -8792) * mm});
            skLineSegment(sketch, "E830", {"start": v(2211.83, -8792) * mm, "end": v(2560.56, -8449.84) * mm});
            skLineSegment(sketch, "E831", {"start": v(2560.56, -8449.84) * mm, "end": v(2898.66, -8121.12) * mm});
            skLineSegment(sketch, "E832", {"start": v(2898.66, -8121.12) * mm, "end": v(3226.08, -7804.32) * mm});
            skLineSegment(sketch, "E833", {"start": v(3226.08, -7804.32) * mm, "end": v(3895.69, -7154.5) * mm});
            skLineSegment(sketch, "E834", {"start": v(3895.69, -7154.5) * mm, "end": v(4518.51, -6535) * mm});
            skLineSegment(sketch, "E835", {"start": v(4518.51, -6535) * mm, "end": v(5095.88, -5929.58) * mm});
            skLineSegment(sketch, "E836", {"start": v(5095.88, -5929.58) * mm, "end": v(5629.12, -5322.05) * mm});
            skLineSegment(sketch, "E837", {"start": v(5629.12, -5322.05) * mm, "end": v(6119.55, -4696.2) * mm});
            skLineSegment(sketch, "E838", {"start": v(6119.55, -4696.2) * mm, "end": v(6568.5, -4035.83) * mm});
            skLineSegment(sketch, "E839", {"start": v(6568.5, -4035.83) * mm, "end": v(6977.3, -3324.73) * mm});
            skLineSegment(sketch, "E840", {"start": v(6977.3, -3324.73) * mm, "end": v(7347.25, -2546.7) * mm});
            skLineSegment(sketch, "E841", {"start": v(7347.25, -2546.7) * mm, "end": v(7684.84, -1666.47) * mm});
            skLineSegment(sketch, "E842", {"start": v(7684.84, -1666.47) * mm, "end": v(7976.8, -698.14) * mm});
            skLineSegment(sketch, "E843", {"start": v(7976.8, -698.14) * mm, "end": v(8224.99, 370.6) * mm});
            skLineSegment(sketch, "E844", {"start": v(8224.99, 370.6) * mm, "end": v(8431.23, 1552.01) * mm});
            skLineSegment(sketch, "E845", {"start": v(8431.23, 1552.01) * mm, "end": v(8597.38, 2858.4) * mm});
            skLineSegment(sketch, "E846", {"start": v(8597.38, 2858.4) * mm, "end": v(8725.27, 4302.03) * mm});
            skLineSegment(sketch, "E847", {"start": v(8725.27, 4302.03) * mm, "end": v(8816.74, 5895.2) * mm});
            skLineSegment(sketch, "E848", {"start": v(8816.74, 5895.2) * mm, "end": v(8873.64, 7650.19) * mm});
            skLineSegment(sketch, "E849", {"start": v(8873.64, 7650.19) * mm, "end": v(8881.7, 8019.28) * mm});
            skLineSegment(sketch, "E850", {"start": v(8881.7, 8019.28) * mm, "end": v(8516.95, 8076.12) * mm});
            skSolve(sketch);
        }
        {
            var Q0;
            Q0 = qSketchRegion(id + "F0", true);
            var Q1;
            Q1=makeQuery(id+"F0.imprint","IMPRINT",FACE,{"disambiguationData":[TD([[makeQuery(id+"F0.imprint","IMPRINT",EDGE,{"derivedFrom":sQuery(id+"F0.wireOp",EDGE,"E464")}),-1.0]])]});
            var Q2;
            Q2=makeQuery(id+"F0.imprint","IMPRINT",FACE,{"disambiguationData":[TD([[makeQuery(id+"F0.imprint","IMPRINT",EDGE,{"derivedFrom":sQuery(id+"F0.wireOp",EDGE,"E0")}),-1.0]])]});
            extrude(context, id + "F1", {"entities" : qUnion([Q0, Q1, Q2]), "depth" : 76.2 * mm, "offsetDistance" : 25.4 * mm});
        }
        {
            var Q0;
            Q0=makeQuery(id+"F1.opExtrude","CAP_FACE",FACE,{"disambiguationData":[OSD([sQuery(id+"F0.wireOp",EDGE,"E778"),sQuery(id+"F0.wireOp",EDGE,"E779"),sQuery(id+"F0.wireOp",EDGE,"E780"),sQuery(id+"F0.wireOp",EDGE,"E781"),sQuery(id+"F0.wireOp",EDGE,"E782"),sQuery(id+"F0.wireOp",EDGE,"E783"),sQuery(id+"F0.wireOp",EDGE,"E784"),sQuery(id+"F0.wireOp",EDGE,"E785"),sQuery(id+"F0.wireOp",EDGE,"E786"),sQuery(id+"F0.wireOp",EDGE,"E787"),sQuery(id+"F0.wireOp",EDGE,"E788"),sQuery(id+"F0.wireOp",EDGE,"E789"),sQuery(id+"F0.wireOp",EDGE,"E790"),sQuery(id+"F0.wireOp",EDGE,"E791"),sQuery(id+"F0.wireOp",EDGE,"E792"),sQuery(id+"F0.wireOp",EDGE,"E793"),sQuery(id+"F0.wireOp",EDGE,"E794"),sQuery(id+"F0.wireOp",EDGE,"E795"),sQuery(id+"F0.wireOp",EDGE,"E796"),sQuery(id+"F0.wireOp",EDGE,"E797"),sQuery(id+"F0.wireOp",EDGE,"E798"),sQuery(id+"F0.wireOp",EDGE,"E799"),sQuery(id+"F0.wireOp",EDGE,"E800"),sQuery(id+"F0.wireOp",EDGE,"E801"),sQuery(id+"F0.wireOp",EDGE,"E802"),sQuery(id+"F0.wireOp",EDGE,"E803"),sQuery(id+"F0.wireOp",EDGE,"E804"),sQuery(id+"F0.wireOp",EDGE,"E805"),sQuery(id+"F0.wireOp",EDGE,"E806"),sQuery(id+"F0.wireOp",EDGE,"E807"),sQuery(id+"F0.wireOp",EDGE,"E808"),sQuery(id+"F0.wireOp",EDGE,"E809"),sQuery(id+"F0.wireOp",EDGE,"E810"),sQuery(id+"F0.wireOp",EDGE,"E811"),sQuery(id+"F0.wireOp",EDGE,"E812"),sQuery(id+"F0.wireOp",EDGE,"E813"),sQuery(id+"F0.wireOp",EDGE,"E814"),sQuery(id+"F0.wireOp",EDGE,"E815"),sQuery(id+"F0.wireOp",EDGE,"E816"),sQuery(id+"F0.wireOp",EDGE,"E817"),sQuery(id+"F0.wireOp",EDGE,"E818"),sQuery(id+"F0.wireOp",EDGE,"E819"),sQuery(id+"F0.wireOp",EDGE,"E820"),sQuery(id+"F0.wireOp",EDGE,"E821"),sQuery(id+"F0.wireOp",EDGE,"E822"),sQuery(id+"F0.wireOp",EDGE,"E823"),sQuery(id+"F0.wireOp",EDGE,"E824"),sQuery(id+"F0.wireOp",EDGE,"E825"),sQuery(id+"F0.wireOp",EDGE,"E826"),sQuery(id+"F0.wireOp",EDGE,"E827"),sQuery(id+"F0.wireOp",EDGE,"E828"),sQuery(id+"F0.wireOp",EDGE,"E829"),sQuery(id+"F0.wireOp",EDGE,"E830"),sQuery(id+"F0.wireOp",EDGE,"E831"),sQuery(id+"F0.wireOp",EDGE,"E832"),sQuery(id+"F0.wireOp",EDGE,"E833"),sQuery(id+"F0.wireOp",EDGE,"E834"),sQuery(id+"F0.wireOp",EDGE,"E835"),sQuery(id+"F0.wireOp",EDGE,"E836"),sQuery(id+"F0.wireOp",EDGE,"E837"),sQuery(id+"F0.wireOp",EDGE,"E838"),sQuery(id+"F0.wireOp",EDGE,"E839"),sQuery(id+"F0.wireOp",EDGE,"E840"),sQuery(id+"F0.wireOp",EDGE,"E841"),sQuery(id+"F0.wireOp",EDGE,"E842"),sQuery(id+"F0.wireOp",EDGE,"E843"),sQuery(id+"F0.wireOp",EDGE,"E844"),sQuery(id+"F0.wireOp",EDGE,"E845"),sQuery(id+"F0.wireOp",EDGE,"E846"),sQuery(id+"F0.wireOp",EDGE,"E847"),sQuery(id+"F0.wireOp",EDGE,"E848"),sQuery(id+"F0.wireOp",EDGE,"E849"),sQuery(id+"F0.wireOp",EDGE,"E850")])],"isStart":false});
            extrude(context, id + "F2", {"entities" : qUnion([Q0]), "operationType" : NewBodyOperationType.ADD, "depth" : 25.4 * mm, "offsetDistance" : 25.4 * mm});
        }
    });
